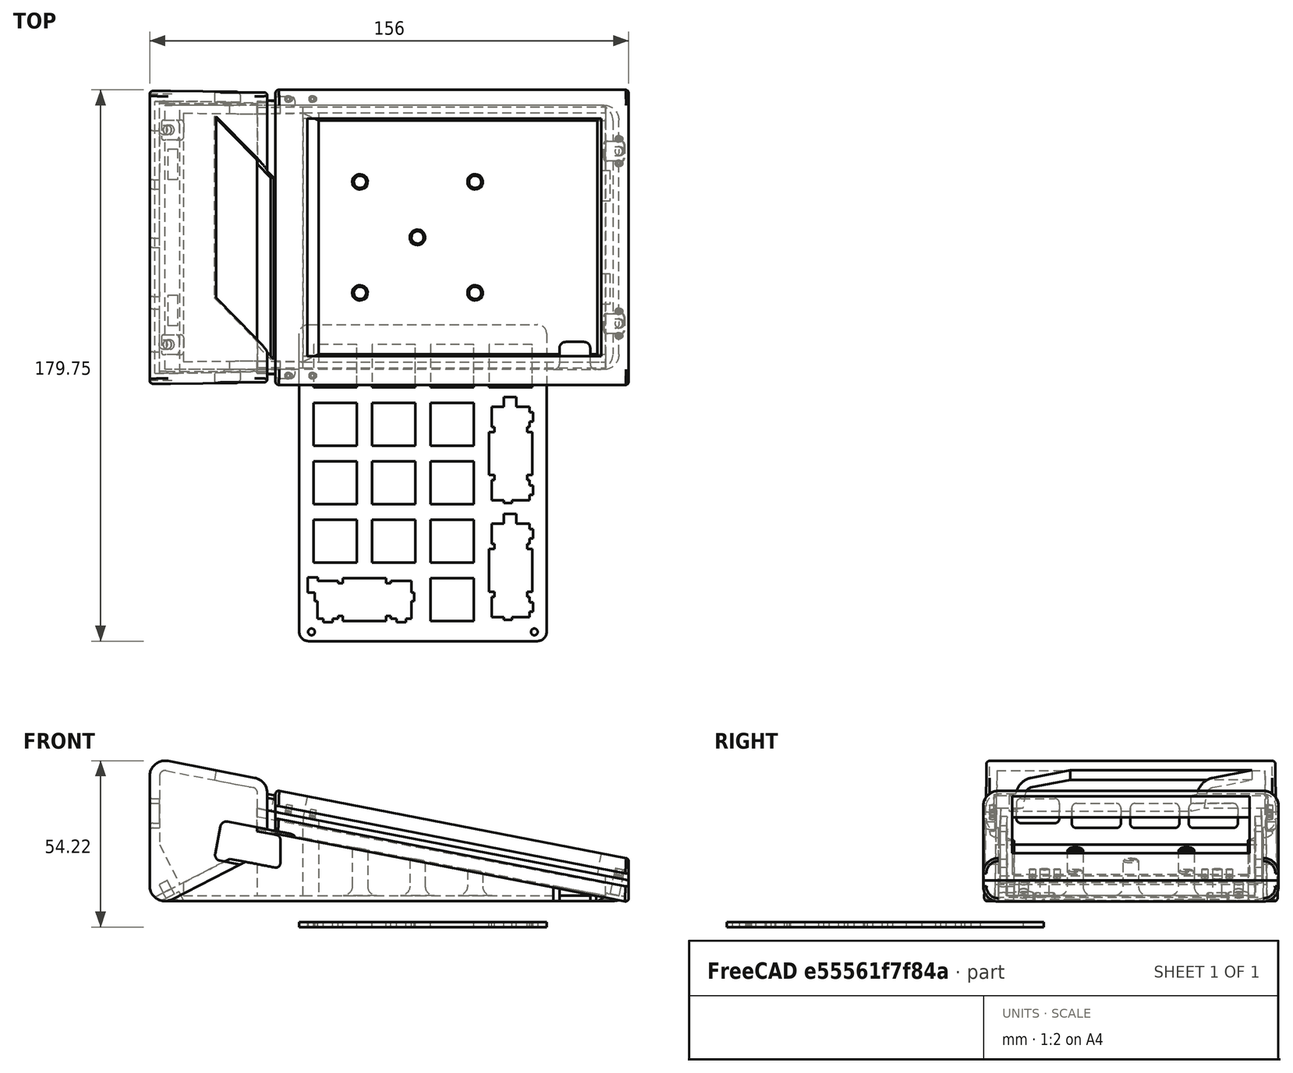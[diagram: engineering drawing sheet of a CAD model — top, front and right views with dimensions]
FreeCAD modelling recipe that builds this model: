
FCSTD DOCUMENT  (FreeCAD 1.0R38806 (Git))
Label: DecenTKL-Numpad-Enclosure
License: All rights reserved
LicenseURL: http://en.wikipedia.org/wiki/All_rights_reserved
objects: Sketcher::SketchObject×35, PartDesign::Pocket×16, PartDesign::Plane×12, PartDesign::Pad×9, PartDesign::SubShapeBinder×8, PartDesign::Point×6, PartDesign::Line×5, Part::Part2DObjectPython×3, App::Part×3, PartDesign::Fillet×3, PartDesign::Body×2, PartDesign::Chamfer×2, PartDesign::Draft×1, Mesh::Feature×1, Part::Feature×1, PartDesign::AdditiveLoft×1, PartDesign::SubtractiveLoft×1
note: 206 computed .brp shape members not serialized (recipe doc carries the construction recipe); baked Part::Feature solids carry a one-line shape summary decoded from their .brp

FEATURE [Sketcher::SketchObject] Sketch  label="ConsoleKeySectionSketch"
  ArcFitTolerance = 0
  AttachmentSupport = -> [XZ_Plane001]
  FullyConstrained = true
  MakeInternals = false
  MapMode = 5
  Placement = pos=(0,0,0) rot=(1,0,0;1.5708rad)
  sketch-geometry (12):
    g0: LineSegment StartX=5.95204 StartY=54.1257 StartZ=0 EndX=34.2385 EndY=48.6393 EndZ=0
    g1: ArcOfCircle CenterX=33.2865 CenterY=43.7308 CenterZ=0 NormalX=0 NormalY=0 NormalZ=1 AngleXU=0 Radius=5 StartAngle=3e-16 EndAngle=1.37922
    g2: LineSegment StartX=38.2865 StartY=43.7308 StartZ=0 EndX=38.2865 EndY=27.9135 EndZ=0
    g3: ArcOfCircle CenterX=33.2865 CenterY=27.9135 CenterZ=0 NormalX=0 NormalY=0 NormalZ=1 AngleXU=0 Radius=5 StartAngle=5.185 EndAngle=6.28319
    g4: LineSegment StartX=35.5625 StartY=23.4615 StartZ=0 EndX=7.27606 EndY=9 EndZ=0
    g5: ArcOfCircle CenterX=5 CenterY=13.4519 CenterZ=0 NormalX=0 NormalY=0 NormalZ=1 AngleXU=0 Radius=5 StartAngle=3.14159 EndAngle=5.185
    g6: LineSegment StartX=1.24e-14 StartY=13.4519 StartZ=0 EndX=1.24e-14 EndY=49.2171 EndZ=0
    g7: ArcOfCircle CenterX=5 CenterY=49.2171 CenterZ=0 NormalX=0 NormalY=0 NormalZ=1 AngleXU=0 Radius=5 StartAngle=1.37922 EndAngle=3.14159
    g8: GeomPoint [constr] X=0 Y=55.2801 Z=0
    g9: GeomPoint [constr] X=38.2865 Y=47.8542 Z=0
    g10: GeomPoint [constr] X=0 Y=5.2801 Z=0
    g11: GeomPoint [constr] X=38.2865 Y=24.8542 Z=0
  constraints (28):
    c: Tangent(g0,g1) = 1.5708
    c: Tangent(g2,g3) = 1.5708
    c: Tangent(g4,g5) = 1.5708
    c: Tangent(g6,g7) = 1.5708
    c: Tangent(g7,g0) = 1.5708
    c: Tangent(g5,g6) = 1.5708
    c: Tangent(g3,g4) = 1.5708
    c: Tangent(g1,g2) = 1.5708
    c: PointOnObject(g8,g0)
    c: PointOnObject(g8,g6)
    c: PointOnObject(g9,g0)
    c: PointOnObject(g9,g2)
    c: PointOnObject(g11,g2)
    c: PointOnObject(g11,g4)
    c: PointOnObject(g10,g4)
    c: PointOnObject(g10,g6)
    c: Distance(g8,g9) = 39
    c: Radius(g1) = 5
    c: Equal(g1,g7)
    c: Equal(g1,g3)
    c: Equal(g1,g5)
    c: Distance(g9,g11) = 23
    c: Distance(g8,g10) = 50
    c: Distance(g10,g11) = 43
    c: Vertical(g6)
    c: Vertical(g2)
    c: DistanceY(g-1,g4) = 9
    c: DistanceX(g-1,g5) = 0
FEATURE [PartDesign::Pad] Pad  label="ConsoleKeySection"
  Direction = (0,-1,2e-16)
  Length = 94
  Length2 = 10
  Placement = pos=(0,0,0) rot=(1,0,0;1.5708rad)
  Profile = -> Sketch
  ReferenceAxis = -> Sketch [N_Axis]
  Suppressed = false
  Type = 0
FEATURE [PartDesign::Draft] Draft  label="KeySectionDraft"
  Angle = 1
  Base = -> Pad [Face10,Face9]
  BaseFeature = -> Pad
  NeutralPlane = -> Pad [Face1]
  Placement = pos=(0,0,0) rot=(1,0,0;1.5708rad)
  SupportTransform = false
  Suppressed = false
FEATURE [PartDesign::Plane] DatumPlane  label="KeyboardSectionBackPlane"
  AttachmentOffset = pos=(0,0,41) rot=(0,0,1;0rad)
  AttachmentSupport = -> [YZ_Plane001]
  Length = 139.608
  MapMode = 2
  Placement = pos=(41,0,0) rot=(0.57735,0.57735,0.57735;2.0944rad)
  ResizeMode = 0
  Width = 98.7235
FEATURE [PartDesign::Line] DatumLine  label="SlopeDatumLineLeft"
  AttacherType = Attacher::AttachEngineLine
  AttachmentSupport = -> [Draft]
  Length = 20
  MapMode = 29
  Placement = pos=(10.3332,-94,53.2759) rot=(0.610836,0.610836,0.503744;2.20832rad)
  ResizeMode = 0
FEATURE [PartDesign::Point] DatumPoint  label="KeyboardSectionBackPlaneAndSlopeIntersectionDatumPointLeft"
  AttacherType = Attacher::AttachEnginePoint
  AttachmentSupport = -> [DatumLine,DatumPlane]
  MapMode = 40
  Placement = pos=(41,-94,47.3279) rot=(0,0,1;0rad)
FEATURE [PartDesign::Line] DatumLine001  label="SlopeDatumLineRight"
  AttacherType = Attacher::AttachEngineLine
  AttachmentSupport = -> [Sketch]
  Length = 20
  MapMode = 29
  Placement = pos=(10.3332,1.18e-14,53.2759) rot=(0.610836,0.610836,0.503744;2.20832rad)
  ResizeMode = 0
FEATURE [PartDesign::Point] DatumPoint001  label="KeyboardSectionBackPlaneAndSlopeIntersectionDatumPointRight"
  AttacherType = Attacher::AttachEnginePoint
  AttachmentSupport = -> [DatumLine001,DatumPlane]
  MapMode = 40
  Placement = pos=(41,1.86e-14,47.3279) rot=(0,0,1;0rad)
FEATURE [Sketcher::SketchObject] Sketch001  label="KeyboardSectionSketch"
  ArcFitTolerance = 0
  AttachmentSupport = -> [DatumPlane]
  ExternalGeometry = -> [DatumPoint,DatumPoint001]
  FullyConstrained = true
  MakeInternals = false
  MapMode = 5
  Placement = pos=(41,0,0) rot=(0.57735,0.57735,0.57735;2.0944rad)
  sketch-geometry (6):
    g0: LineSegment StartX=-95.1 StartY=37.5279 StartZ=0 EndX=1.1 EndY=37.5279 EndZ=0
    g1: LineSegment StartX=1.1 StartY=37.5279 StartZ=0 EndX=1.1 EndY=39.6279 EndZ=0
    g2: LineSegment StartX=-95.1 StartY=37.5279 StartZ=0 EndX=-95.1 EndY=39.6279 EndZ=0
    g3: ArcOfCircle CenterX=-90.1 CenterY=39.6279 CenterZ=0 NormalX=0 NormalY=0 NormalZ=1 AngleXU=0 Radius=5 StartAngle=1.5708 EndAngle=3.14159
    g4: ArcOfCircle CenterX=-3.9 CenterY=39.6279 CenterZ=0 NormalX=0 NormalY=0 NormalZ=1 AngleXU=0 Radius=5 StartAngle=0 EndAngle=1.5708
    g5: LineSegment StartX=-90.1 StartY=44.6279 StartZ=0 EndX=-3.9 EndY=44.6279 EndZ=0
  constraints (20):
    c: Horizontal(g0)
    c: Coincident(g1,g0)
    c: Vertical(g1)
    c: Coincident(g2,g0)
    c: Vertical(g2)
    c: Coincident(g3,g2)
    c: Coincident(g4,g1)
    c: Coincident(g5,g3)
    c: Coincident(g5,g4)
    c: Horizontal(g5)
    c: Vertical(g3,g3)
    c: Vertical(g4,g4)
    c: Horizontal(g2,g3)
    c: Horizontal(g4,g1)
    c: Equal(g2,g1)
    c: Radius(g4) = 5
    c: DistanceX(g2,g-3) = 1.1
    c: DistanceX(g-4,g1) = 1.1
    c: DistanceY(g0,g3) = 7.1
    c: DistanceY(g3,g-3) = 2.7
FEATURE [Sketcher::SketchObject] Sketch002  label="ConsoleToKEyboardSectionJoinSketch"
  ArcFitTolerance = 0
  AttachmentSupport = -> [DatumPlane]
  ExternalGeometry = -> [Sketch001]
  FullyConstrained = true
  MakeInternals = false
  MapMode = 5
  Placement = pos=(41,0,0) rot=(0.57735,0.57735,0.57735;2.0944rad)
  sketch-geometry (8):
    g0: LineSegment StartX=-91.6 StartY=37.5279 StartZ=0 EndX=-2.4 EndY=37.5279 EndZ=0
    g1: LineSegment StartX=-90.4 StartY=42.8279 StartZ=0 EndX=-3.6 EndY=42.8279 EndZ=0
    g2: LineSegment [constr] StartX=-95.1 StartY=37.5279 StartZ=0 EndX=-91.6 EndY=37.5279 EndZ=0
    g3: LineSegment [constr] StartX=-2.4 StartY=37.5279 StartZ=0 EndX=1.1 EndY=37.5279 EndZ=0
    g4: ArcOfCircle CenterX=-90.4 CenterY=41.6279 CenterZ=0 NormalX=0 NormalY=0 NormalZ=1 AngleXU=0 Radius=1.2 StartAngle=1.5708 EndAngle=3.14159
    g5: LineSegment StartX=-91.6 StartY=37.5279 StartZ=0 EndX=-91.6 EndY=41.6279 EndZ=0
    g6: ArcOfCircle CenterX=-3.6 CenterY=41.6279 CenterZ=0 NormalX=0 NormalY=0 NormalZ=1 AngleXU=0 Radius=1.2 StartAngle=1.1e-15 EndAngle=1.5708
    g7: LineSegment StartX=-2.4 StartY=41.6279 StartZ=0 EndX=-2.4 EndY=37.5279 EndZ=0
  constraints (24):
    c: PointOnObject(g0,g-3)
    c: PointOnObject(g0,g-3)
    c: Horizontal(g1)
    c: DistanceX(g-3,g0) = 3.5
    c: Coincident(g2,g-3)
    c: Coincident(g2,g0)
    c: Coincident(g3,g0)
    c: Coincident(g3,g-3)
    c: Vertical(g4,g4)
    c: Coincident(g4,g1)
    c: Vertical(g4,g0)
    c: Horizontal(g4,g4)
    c: Radius(g4) = 1.2
    c: Coincident(g5,g0)
    c: Coincident(g5,g4)
    c: Equal(g4,g6)
    c: Horizontal(g6,g6)
    c: Vertical(g6,g6)
    c: Vertical(g0,g6)
    c: Coincident(g1,g6)
    c: Coincident(g7,g6)
    c: Coincident(g7,g0)
    c: Equal(g2,g3)
    c: DistanceY(g0,g1) = 5.3
FEATURE [PartDesign::Pad] Pad001  label="ConsoleToKeyboardSectionJoin"
  BaseFeature = -> Draft
  Direction = (0.981705,0,-0.190408)
  Length = 10
  Length2 = 10
  Placement = pos=(0,0,0) rot=(1,0,0;1.5708rad)
  Profile = -> Sketch002
  ReferenceAxis = -> DatumLine
  Reversed = true
  Suppressed = false
  Type = 3
  UpToFace = -> Draft [Face3]
FEATURE [PartDesign::Pad] Pad002  label="KeyboardSectionPad"
  BaseFeature = -> Pad001
  Direction = (0.981705,0,-0.190408)
  Length = 115
  Length2 = 10
  Placement = pos=(0,0,0) rot=(1,0,0;1.5708rad)
  Profile = -> Sketch001
  ReferenceAxis = -> DatumLine
  Suppressed = false
  Type = 0
FEATURE [PartDesign::Plane] DatumPlane001  label="ConsoleSectionLeftInnerPlane"
  AttachmentOffset = pos=(0,0,-3.4) rot=(0,0,1;0rad)
  AttachmentSupport = -> [Draft]
  Length = 205.685
  MapMode = 5
  Placement = pos=(0.304171,-91.5189,1.56824) rot=(0.999997,0.00169,0.001662;1.55367rad)
  ResizeMode = 0
  Width = 105.544
FEATURE [PartDesign::Plane] DatumPlane002  label="ConsoleSectionRightInnerPlane"
  AttachmentOffset = pos=(0,0,-3.4) rot=(0,0,1;0rad)
  AttachmentSupport = -> [Draft]
  Length = 205.685
  MapMode = 5
  Placement = pos=(-0.00815113,-2.45251,-0.0420255) rot=(-0.999997,0.00169,-0.001662;1.55367rad)
  ResizeMode = 0
  Width = 105.544
FEATURE [Sketcher::SketchObject] Sketch003  label="ConsoleSectionCavitySketch"
  ArcFitTolerance = 0
  AttachmentOffset = pos=(0,0,10) rot=(0,0,1;0rad)
  AttachmentSupport = -> [XZ_Plane001]
  ExternalGeometry = -> [Sketch,Pad001]
  FullyConstrained = true
  MakeInternals = false
  MapMode = 5
  Placement = pos=(0,-10,2.2e-15) rot=(1,0,0;1.5708rad)
  sketch-geometry (22):
    g0: ArcOfCircle CenterX=5 CenterY=49.2171 CenterZ=0 NormalX=0 NormalY=0 NormalZ=1 AngleXU=0 Radius=1.8 StartAngle=1.37922 EndAngle=3.14159
    g1: LineSegment [constr] StartX=0 StartY=49.2171 StartZ=0 EndX=5 EndY=49.2171 EndZ=0
    g2: LineSegment [constr] StartX=5 StartY=49.2171 StartZ=0 EndX=5.95204 EndY=54.1257 EndZ=0
    g3: LineSegment [constr] StartX=5.95204 StartY=54.1257 StartZ=0 EndX=34.2385 EndY=48.6393 EndZ=0
    g4: LineSegment [constr] StartX=33.2865 StartY=43.7308 StartZ=0 EndX=34.2385 EndY=48.6393 EndZ=0
    g5: LineSegment [constr] StartX=33.2865 StartY=43.7308 StartZ=0 EndX=38.2865 EndY=43.7308 EndZ=0
    g6: ArcOfCircle CenterX=33.2865 CenterY=43.7308 CenterZ=0 NormalX=0 NormalY=0 NormalZ=1 AngleXU=0 Radius=1.8 StartAngle=-8.9e-15 EndAngle=1.37922
    g7: LineSegment StartX=5.34274 StartY=50.9842 StartZ=0 EndX=33.6292 EndY=45.4978 EndZ=0
    g8: LineSegment [constr] StartX=1.24e-14 StartY=13.4519 StartZ=0 EndX=5 EndY=13.4519 EndZ=0
    g9: LineSegment [constr] StartX=5 StartY=13.4519 StartZ=0 EndX=7.27606 EndY=9 EndZ=0
    g10: LineSegment [constr] StartX=33.2865 StartY=27.9135 StartZ=0 EndX=38.2865 EndY=27.9135 EndZ=0
    g11: LineSegment [constr] StartX=33.2865 StartY=27.9135 StartZ=0 EndX=35.5625 EndY=23.4615 EndZ=0
    g12: LineSegment StartX=3.2 StartY=49.2171 StartZ=0 EndX=3.2 EndY=26.8416 EndZ=0
    g13: LineSegment [constr] StartX=7.27606 StartY=9 StartZ=0 EndX=35.5625 EndY=23.4615 EndZ=0
    g14: LineSegment StartX=-17.3575 StartY=0 StartZ=0 EndX=41 EndY=0 EndZ=0
    g15: LineSegment StartX=41 StartY=37.5279 StartZ=0 EndX=41 EndY=0 EndZ=0
    g16: LineSegment StartX=41 StartY=37.5279 StartZ=0 EndX=35.0865 EndY=38.6748 EndZ=0
    g17: LineSegment StartX=35.0865 StartY=38.6748 StartZ=0 EndX=35.0865 EndY=43.7308 EndZ=0
    g18: GeomPoint [constr] X=5.81938 Y=11.8492 Z=0
    g19: LineSegment [constr] StartX=5.81938 StartY=11.8492 StartZ=0 EndX=34.1059 EndY=26.3108 EndZ=0
    g20: LineSegment StartX=-17.3575 StartY=0 StartZ=0 EndX=9.81938 EndY=13.8942 EndZ=0
    g21: LineSegment StartX=3.2 StartY=26.8416 StartZ=0 EndX=9.81938 EndY=13.8942 EndZ=0
  constraints (54):
    c: Coincident(g0,g-3)
    c: Coincident(g1,g-3)
    c: Coincident(g1,g0)
    c: Coincident(g2,g0)
    c: Coincident(g2,g-3)
    c: Coincident(g3,g2)
    c: Coincident(g3,g-4)
    c: Coincident(g4,g-4)
    c: Coincident(g4,g3)
    c: Coincident(g5,g4)
    c: Coincident(g5,g-4)
    c: PointOnObject(g0,g2)
    c: PointOnObject(g0,g1)
    c: DistanceX(g1,g0) = 3.2
    c: Coincident(g6,g4)
    c: PointOnObject(g6,g4)
    c: PointOnObject(g6,g5)
    c: DistanceX(g6,g5) = 3.2
    c: Coincident(g7,g0)
    c: Coincident(g7,g6)
    c: Coincident(g8,g-6)
    c: Coincident(g8,g-6)
    c: Coincident(g9,g8)
    c: Coincident(g9,g-6)
    c: Coincident(g10,g-5)
    c: Coincident(g10,g-5)
    c: Coincident(g11,g10)
    c: Coincident(g11,g-5)
    c: DistanceX(g8,g12) = 3.2
    c: Coincident(g12,g0)
    c: Coincident(g13,g9)
    c: Coincident(g13,g11)
    c: Horizontal(g14)
    c: Coincident(g15,g14)
    c: Vertical(g15)
    c: Coincident(g15,g-7)
    c: Coincident(g16,g15)
    c: Coincident(g17,g16)
    c: Coincident(g17,g6)
    c: Vertical(g17)
    c: PointOnObject(g16,g-7)
    c: PointOnObject(g18,g9)
    c: Distance(g18,g9) = 3.2
    c: Coincident(g19,g18)
    c: PointOnObject(g19,g11)
    c: Parallel(g19,g13)
    c: PointOnObject(g14,g19)
    c: Coincident(g20,g14)
    c: PointOnObject(g14,g-1)
    c: PointOnObject(g20,g19)
    c: Coincident(g21,g12)
    c: Coincident(g21,g20)
    c: Parallel(g21,g9)
    c: DistanceX(g18,g20) = 4
FEATURE [PartDesign::Pocket] Pocket  label="ConsoleKeyCavityPocketRight"
  BaseFeature = -> Pad002
  Direction = (0,1,-2e-16)
  Length = 0
  Length2 = 5
  Placement = pos=(0,0,0) rot=(1,0,0;1.5708rad)
  Profile = -> Sketch003
  ReferenceAxis = -> Sketch003 [N_Axis]
  Refine = true
  Reversed = true
  Suppressed = false
  Type = 3
  UpToFace = -> DatumPlane001 [Plane]
FEATURE [PartDesign::Pocket] Pocket001  label="ConsoleKeyCavityPocketLeft"
  BaseFeature = -> Pocket
  Direction = (0,1,-2e-16)
  Length = 0
  Length2 = 5
  Placement = pos=(0,0,0) rot=(1,0,0;1.5708rad)
  Profile = -> Sketch003
  ReferenceAxis = -> Sketch003 [N_Axis]
  Refine = true
  Suppressed = false
  Type = 3
  UpToFace = -> DatumPlane002 [Plane]
FEATURE [PartDesign::Plane] DatumPlane003  label="KeyboardSlopeDatumPlane"
  AttachmentSupport = -> [DatumLine001,DatumLine]
  Length = 150.532
  MapMode = 13
  Placement = pos=(10.6605,-31.3333,53.2124) rot=(0.095208,0.095208,0.990894;1.57994rad)
  ResizeMode = 0
  Width = 223.203
FEATURE [Sketcher::SketchObject] Sketch004  label="KeyboardCutoutSketch"
  ArcFitTolerance = 0
  AttachmentSupport = -> [DatumPlane003]
  ExternalGeometry = -> [DatumPoint001,DatumPoint]
  FullyConstrained = true
  MakeInternals = false
  MapMode = 5
  Placement = pos=(10.6605,-31.3333,53.2124) rot=(0.095208,0.095208,0.990894;1.57994rad)
  expr: Constraints[23] = 19.05 * 3 + 2
  sketch-geometry (11):
    g0: LineSegment StartX=-54.3917 StartY=-41.9049 StartZ=0 EndX=23.0583 EndY=-41.9049 EndZ=0
    g1: LineSegment StartX=23.0583 StartY=-41.9049 StartZ=0 EndX=23.0583 EndY=-139.505 EndZ=0
    g2: LineSegment StartX=23.0583 StartY=-139.505 StartZ=0 EndX=-54.3917 EndY=-139.505 EndZ=0
    g3: LineSegment StartX=-54.3917 StartY=-139.505 StartZ=0 EndX=-54.3917 EndY=-41.9049 EndZ=0
    g4: GeomPoint [constr] X=-15.6667 Y=-139.505 Z=0
    g5: LineSegment [constr] StartX=-15.6667 StartY=-139.505 StartZ=0 EndX=-15.6667 EndY=-30.9049 EndZ=0
    g6: LineSegment [constr] StartX=-62.6667 StartY=-30.9049 StartZ=0 EndX=31.3333 EndY=-30.9049 EndZ=0
    g7: LineSegment StartX=-55.3917 StartY=-31.2049 StartZ=0 EndX=-35.3917 EndY=-11.2049 EndZ=0
    g8: LineSegment StartX=-35.3917 StartY=-11.2049 StartZ=0 EndX=23.7583 EndY=-11.2049 EndZ=0
    g9: LineSegment StartX=23.7583 StartY=-11.2049 StartZ=0 EndX=3.75833 EndY=-31.2049 EndZ=0
    g10: LineSegment StartX=3.75833 StartY=-31.2049 StartZ=0 EndX=-55.3917 EndY=-31.2049 EndZ=0
  constraints (29):
    c: Horizontal(g0)
    c: Coincident(g0,g1)
    c: Vertical(g1)
    c: Coincident(g3,g0)
    c: Vertical(g3)
    c: DistanceY(g0,g-3) = 11
    c: DistanceY(g2,g0) = 97.6
    c: DistanceX(g0,g0) = 77.45
    c: Coincident(g2,g3)
    c: Coincident(g2,g1)
    c: Coincident(g5,g4)
    c: Coincident(g6,g-4)
    c: Coincident(g6,g-3)
    c: PointOnObject(g5,g6)
    c: Symmetric(g6,g6,g5)
    c: Coincident(g7,g8)
    c: Horizontal(g8)
    c: Coincident(g8,g9)
    c: Coincident(g9,g10)
    c: Coincident(g10,g7)
    c: Horizontal(g10)
    c: Angle(g10,g7) = 0.785398
    c: Angle(g8,g9) = 0.785398
    c: DistanceX(g8,g8) = 59.15
    c: DistanceX(g7,g0) = 1
    c: DistanceY(g9,g8) = 20
    c: Symmetric(g2,g1,g5)
    c: DistanceY(g0,g7) = 10.7
    c: PointOnObject(g4,g2)
FEATURE [PartDesign::Pocket] Pocket002  label="KeyboardCutout"
  BaseFeature = -> Pocket001
  Direction = (-0.190408,-2e-16,-0.981705)
  Length = 10
  Length2 = 5
  Placement = pos=(0,0,0) rot=(1,0,0;1.5708rad)
  Profile = -> Sketch004
  ReferenceAxis = -> Sketch004 [N_Axis]
  Refine = true
  Suppressed = false
  Type = 0
FEATURE [Sketcher::SketchObject] Sketch008  label="Screw holes sketch"
  ArcFitTolerance = 0
  AttachmentSupport = -> [Pad002]
  ExternalGeometry = -> [Pad002]
  FullyConstrained = true
  MakeInternals = false
  MapMode = 5
  Placement = pos=(8.50136,9.8e-15,43.8312) rot=(0.995416,0,-0.095643;3.14159rad)
  sketch-geometry (11):
    g0: Circle CenterX=146.747 CenterY=75.1 CenterZ=0 NormalX=0 NormalY=0 NormalZ=1 AngleXU=0 Radius=1.5
    g1: Circle CenterX=146.747 CenterY=18.9 CenterZ=0 NormalX=0 NormalY=0 NormalZ=1 AngleXU=0 Radius=1.5
    g2: Circle CenterX=146.747 CenterY=79.1 CenterZ=0 NormalX=0 NormalY=0 NormalZ=1 AngleXU=0 Radius=1
    g3: Circle CenterX=146.747 CenterY=71.1 CenterZ=0 NormalX=0 NormalY=0 NormalZ=1 AngleXU=0 Radius=1
    g4: Circle CenterX=37.1043 CenterY=92.1 CenterZ=0 NormalX=0 NormalY=0 NormalZ=1 AngleXU=0 Radius=1
    g5: Circle CenterX=45.1043 CenterY=92.1 CenterZ=0 NormalX=0 NormalY=0 NormalZ=1 AngleXU=0 Radius=1
    g6: Circle CenterX=146.747 CenterY=22.9 CenterZ=0 NormalX=0 NormalY=0 NormalZ=1 AngleXU=0 Radius=1
    g7: Circle CenterX=146.747 CenterY=14.9 CenterZ=0 NormalX=0 NormalY=0 NormalZ=1 AngleXU=0 Radius=1
    g8: Circle CenterX=45.1043 CenterY=1.9 CenterZ=0 NormalX=0 NormalY=0 NormalZ=1 AngleXU=0 Radius=1
    g9: Circle CenterX=37.1043 CenterY=1.9 CenterZ=0 NormalX=0 NormalY=0 NormalZ=1 AngleXU=0 Radius=1
    g10: LineSegment [constr] StartX=33.1043 StartY=47 StartZ=0 EndX=150.247 EndY=47 EndZ=0
  constraints (28):
    c: Vertical(g2,g0)
    c: Symmetric(g2,g3,g0)
    c: DistanceY(g3,g2) = 8
    c: Equal(g2,g3)
    c: Equal(g2,g5)
    c: Equal(g5,g4)
    c: DistanceX(g4,g5) = 8
    c: Vertical(g6,g1)
    c: Symmetric(g6,g7,g1)
    c: DistanceY(g7,g6) = 8
    c: Equal(g6,g7)
    c: Equal(g6,g8)
    c: Equal(g8,g9)
    c: DistanceX(g9,g8) = 8
    c: Symmetric(g0,g1,g10)
    c: Symmetric(g-4,g-3,g10)
    c: Symmetric(g-4,g-3,g10)
    c: DistanceX(g1,g-4) = 3.5
    c: DistanceY(g-4,g1) = 20
    c: Diameter(g5) = 2
    c: Equal(g5,g8)
    c: Horizontal(g9,g8)
    c: Horizontal(g4,g5)
    c: Symmetric(g4,g9,g10)
    c: DistanceY(g9,g4) = 90.2
    c: DistanceX(g-4,g9) = 4
    c: Equal(g0,g1)
    c: Radius(g1) = 1.5
FEATURE [Part::Part2DObjectPython] Shape2DView  label="Key Cutout Projection"  # Draft 2D object (typed FeaturePython)
  AutoUpdate = true
  Base = -> Sketch004
  Clip = false
  FuseArch = false
  HiddenLines = false
  InPlace = true
  OnlySolids = false
  Projection = (0.190408,0,0.981705)
  ProjectionMode = 0
  SegmentLength = 0.05
  Tessellation = false
  VisibleOnly = false
FEATURE [PartDesign::SubShapeBinder] Binder007  label="Slope binder"
  BindCopyOnChange = 0
  BindMode = 0
  ClaimChildren = false
  Context = -> Part001 [Body001.Binder007.]
  Fuse = false
  MakeFace = true
  OffsetFill = false
  OffsetIntersection = false
  OffsetJoinType = 0
  OffsetOpenResult = false
  PartialLoad = false
  Relative = true
  Support = -> [Part[Body.DatumLine001.]]
  _Version = 2
FEATURE [PartDesign::SubShapeBinder] Binder011  label="Top console to keyboard binder"
  BindCopyOnChange = 0
  BindMode = 0
  ClaimChildren = false
  Context = -> Part001 [Body001.Binder011.]
  Fuse = false
  MakeFace = true
  OffsetFill = false
  OffsetIntersection = false
  OffsetJoinType = 0
  OffsetOpenResult = false
  PartialLoad = false
  Relative = true
  Support = -> [Part[Body.Pad001.Face17]]
  _Version = 2
FEATURE [PartDesign::SubShapeBinder] Binder013  label="Screw holes binder"
  BindCopyOnChange = 0
  BindMode = 0
  ClaimChildren = false
  Context = -> Part001 [Body001.Binder013.]
  Fuse = false
  MakeFace = true
  OffsetFill = false
  OffsetIntersection = false
  OffsetJoinType = 0
  OffsetOpenResult = false
  PartialLoad = false
  Relative = true
  Support = -> [Part[Body.Pocket005.Sketch008.]]
  _Version = 2
FEATURE [Mesh::Feature] DecentNumPad
  Placement = pos=(-11.8196,-113,42.0954) rot=(0.095409,0.095409,0.990855;1.57998rad)
FEATURE [Part::Feature] Part__Feature  label="NumPadPlate_PCB"
  shape: bbox 80.58 x 103.2 x 1.6 mm, 178 faces (baked)
FEATURE [App::Part] NumPadPlate_1  label="NumPadPlate 1"
  Group = -> [Part__Feature]
  Origin = -> Origin005
  Placement = pos=(-27.275,-136,49.1) rot=(0.095409,0.095409,0.990855;1.57998rad)
FEATURE [PartDesign::SubShapeBinder] Binder  label="PlateBinder"
  BindCopyOnChange = 0
  BindMode = 0
  ClaimChildren = false
  Context = -> Part [Body.Binder.]
  Fuse = false
  MakeFace = true
  OffsetFill = false
  OffsetIntersection = false
  OffsetJoinType = 0
  OffsetOpenResult = false
  PartialLoad = false
  Relative = true
  Support = -> [NumPadPlate_1[Part__Feature.]]
  _Version = 2
FEATURE [PartDesign::Plane] DatumPlane010  label="TopOfPlatePlane"
  AttachmentSupport = -> [Binder]
  Length = 223.222
  MapMode = 5
  Placement = pos=(8.50886,0,43.7743) rot=(0,1,0;0.191986rad)
  ResizeMode = 0
  Width = 150.533
FEATURE [PartDesign::Line] DatumLine005  label="Right PCB edge"
  AttacherType = Attacher::AttachEngineLine
  AttachmentOffset = pos=(0,-3,0) rot=(0,0,1;0rad)
  AttachmentSupport = -> [Binder]
  Length = 20
  MapMode = 29
  Placement = pos=(7.63113,-6.7,39.2588) rot=(0.610901,0.610901,0.503588;2.20857rad)
  ResizeMode = 0
FEATURE [PartDesign::Line] DatumLine006  label="Left PCB edge"
  AttacherType = Attacher::AttachEngineLine
  AttachmentOffset = pos=(0,-3,0) rot=(0,0,1;0rad)
  AttachmentSupport = -> [Binder]
  Length = 20
  MapMode = 29
  Placement = pos=(7.63113,-87.2812,39.2588) rot=(0.536704,-0.536704,-0.651074;1.98733rad)
  ResizeMode = 0
FEATURE [PartDesign::Plane] DatumPlane011  label="Back plane"
  AttachmentSupport = -> [Pad]
  Length = 98.7235
  MapMode = 5
  Placement = pos=(1.24e-14,0,0) rot=(0.707107,0,-0.707107;3.14159rad)
  ResizeMode = 0
  Width = 139.608
FEATURE [PartDesign::Point] DatumPoint002  label="Back PCB top plane right intersection"
  AttacherType = Attacher::AttachEnginePoint
  AttachmentSupport = -> [DatumPlane011,DatumLine005]
  MapMode = 40
  Placement = pos=(3.6e-15,-6.7,40.7421) rot=(0,0,1;0rad)
FEATURE [PartDesign::Point] DatumPoint003  label="Back PCB top plane left intersection"
  AttacherType = Attacher::AttachEnginePoint
  AttachmentSupport = -> [DatumPlane011,DatumLine006]
  MapMode = 40
  Placement = pos=(3.6e-15,-87.2812,40.7421) rot=(0,0,1;0rad)
FEATURE [Sketcher::SketchObject] Sketch006  label="USB Port Sketch"
  ArcFitTolerance = 0
  AttachmentSupport = -> [Pad]
  ExternalGeometry = -> [DatumPoint003,DatumPoint002]
  FullyConstrained = true
  MakeInternals = false
  MapMode = 5
  Placement = pos=(1.24e-14,0,0) rot=(0.707107,0,-0.707107;3.14159rad)
  sketch-geometry (38):
    g0: ArcOfCircle CenterX=-40.3621 CenterY=82.8112 CenterZ=0 NormalX=0 NormalY=0 NormalZ=1 AngleXU=0 Radius=1.5 StartAngle=1.5708 EndAngle=3.14159
    g1: LineSegment StartX=-40.3621 StartY=84.3112 StartZ=0 EndX=-35.3621 EndY=84.3112 EndZ=0
    g2: ArcOfCircle CenterX=-35.3621 CenterY=82.8112 CenterZ=0 NormalX=0 NormalY=0 NormalZ=1 AngleXU=0 Radius=1.5 StartAngle=-3.6e-15 EndAngle=1.5708
    g3: LineSegment StartX=-33.8621 StartY=82.8112 StartZ=0 EndX=-33.8621 EndY=71.8113 EndZ=0
    g4: ArcOfCircle CenterX=-35.3621 CenterY=71.8112 CenterZ=0 NormalX=0 NormalY=0 NormalZ=1 AngleXU=0 Radius=1.5 StartAngle=4.71239 EndAngle=6.28319
    g5: LineSegment StartX=-35.3621 StartY=70.3112 StartZ=0 EndX=-40.3621 EndY=70.3112 EndZ=0
    g6: ArcOfCircle CenterX=-40.3621 CenterY=71.8112 CenterZ=0 NormalX=0 NormalY=0 NormalZ=1 AngleXU=0 Radius=1.5 StartAngle=3.14159 EndAngle=4.71239
    g7: LineSegment StartX=-41.8621 StartY=71.8112 StartZ=0 EndX=-41.8621 EndY=82.8112 EndZ=0
    g8: GeomPoint [constr] X=-37.8621 Y=77.3112 Z=0
    g9: ArcOfCircle CenterX=-38.7821 CenterY=51.7612 CenterZ=0 NormalX=0 NormalY=0 NormalZ=1 AngleXU=0 Radius=1.5 StartAngle=3.14159 EndAngle=4.71239
    g10: LineSegment StartX=-40.2821 StartY=51.7612 StartZ=0 EndX=-40.2821 EndY=64.7612 EndZ=0
    g11: ArcOfCircle CenterX=-38.7821 CenterY=64.7612 CenterZ=0 NormalX=0 NormalY=0 NormalZ=1 AngleXU=0 Radius=1.5 StartAngle=1.5708 EndAngle=3.14159
    g12: LineSegment StartX=-38.7821 StartY=66.2612 StartZ=0 EndX=-33.7821 EndY=66.2612 EndZ=0
    g13: ArcOfCircle CenterX=-33.7821 CenterY=64.7612 CenterZ=0 NormalX=0 NormalY=0 NormalZ=1 AngleXU=0 Radius=1.5 StartAngle=4.6e-15 EndAngle=1.5708
    g14: LineSegment StartX=-32.2821 StartY=64.7612 StartZ=0 EndX=-32.2821 EndY=51.7612 EndZ=0
    g15: ArcOfCircle CenterX=-33.7821 CenterY=51.7612 CenterZ=0 NormalX=0 NormalY=0 NormalZ=1 AngleXU=0 Radius=1.5 StartAngle=4.71239 EndAngle=6.28319
    g16: LineSegment StartX=-33.7821 StartY=50.2612 StartZ=0 EndX=-38.7821 EndY=50.2612 EndZ=0
    g17: GeomPoint [constr] X=-40.2821 Y=50.2612 Z=0
    g18: GeomPoint [constr] X=-32.2821 Y=66.2613 Z=0
    g19: GeomPoint [constr] X=-36.2821 Y=58.2612 Z=0
    g20: ArcOfCircle CenterX=-38.7821 CenterY=45.7112 CenterZ=0 NormalX=0 NormalY=0 NormalZ=1 AngleXU=0 Radius=1.5 StartAngle=1.5708 EndAngle=3.14159
    g21: LineSegment StartX=-38.7821 StartY=47.2112 StartZ=0 EndX=-33.7821 EndY=47.2112 EndZ=0
    g22: ArcOfCircle CenterX=-33.7821 CenterY=45.7112 CenterZ=0 NormalX=0 NormalY=0 NormalZ=1 AngleXU=0 Radius=1.5 StartAngle=0 EndAngle=1.5708
    g23: LineSegment StartX=-32.2821 StartY=45.7112 StartZ=0 EndX=-32.2821 EndY=32.7112 EndZ=0
    g24: ArcOfCircle CenterX=-33.7821 CenterY=32.7112 CenterZ=0 NormalX=0 NormalY=0 NormalZ=1 AngleXU=0 Radius=1.5 StartAngle=4.71239 EndAngle=6.28319
    g25: LineSegment StartX=-33.7821 StartY=31.2112 StartZ=0 EndX=-38.7821 EndY=31.2112 EndZ=0
    g26: ArcOfCircle CenterX=-38.7821 CenterY=32.7112 CenterZ=0 NormalX=0 NormalY=0 NormalZ=1 AngleXU=0 Radius=1.5 StartAngle=3.14159 EndAngle=4.71239
    g27: LineSegment StartX=-40.2821 StartY=32.7112 StartZ=0 EndX=-40.2821 EndY=45.7112 EndZ=0
    g28: GeomPoint [constr] X=-36.2821 Y=39.2112 Z=0
    g29: ArcOfCircle CenterX=-38.7821 CenterY=26.6612 CenterZ=0 NormalX=0 NormalY=0 NormalZ=1 AngleXU=0 Radius=1.5 StartAngle=1.5708 EndAngle=3.14159
    g30: GeomPoint [constr] X=-36.2821 Y=20.1612 Z=0
    g31: LineSegment StartX=-38.7821 StartY=28.1612 StartZ=0 EndX=-33.7821 EndY=28.1612 EndZ=0
    g32: ArcOfCircle CenterX=-33.7821 CenterY=26.6612 CenterZ=0 NormalX=0 NormalY=0 NormalZ=1 AngleXU=0 Radius=1.5 StartAngle=1e-15 EndAngle=1.5708
    g33: LineSegment StartX=-32.2821 StartY=26.6612 StartZ=0 EndX=-32.2821 EndY=13.6612 EndZ=0
    g34: ArcOfCircle CenterX=-33.7821 CenterY=13.6612 CenterZ=0 NormalX=0 NormalY=0 NormalZ=1 AngleXU=0 Radius=1.5 StartAngle=4.71239 EndAngle=6.28319
    g35: LineSegment StartX=-33.7821 StartY=12.1612 StartZ=0 EndX=-38.7821 EndY=12.1612 EndZ=0
    g36: ArcOfCircle CenterX=-38.7821 CenterY=13.6612 CenterZ=0 NormalX=0 NormalY=0 NormalZ=1 AngleXU=0 Radius=1.5 StartAngle=3.14159 EndAngle=4.71239
    g37: LineSegment StartX=-40.2821 StartY=13.6612 StartZ=0 EndX=-40.2821 EndY=26.6612 EndZ=0
  constraints (88):
    c: Tangent(g0,g1) = 1.5708
    c: Tangent(g1,g2) = 1.5708
    c: Tangent(g2,g3) = 1.5708
    c: Tangent(g3,g4) = 1.5708
    c: Tangent(g4,g5) = 1.5708
    c: Tangent(g5,g6) = 1.5708
    c: Tangent(g6,g7) = 1.5708
    c: Tangent(g7,g0) = 1.5708
    c: Horizontal(g1)
    c: Horizontal(g5)
    c: Vertical(g3)
    c: Vertical(g7)
    c: Equal(g0,g2)
    c: Equal(g2,g4)
    c: Equal(g4,g6)
    c: Diameter(g0) = 3
    c: DistanceX(g6,g3) = 8
    c: DistanceY(g4,g1) = 14
    c: Symmetric(g0,g4,g8)
    c: DistanceX(g-4,g8) = 2.88
    c: Tangent(g9,g10) = 1.5708
    c: Tangent(g10,g11) = 1.5708
    c: Tangent(g11,g12) = 1.5708
    c: Tangent(g12,g13) = 1.5708
    c: Tangent(g13,g14) = 1.5708
    c: Tangent(g14,g15) = 1.5708
    c: Tangent(g15,g16) = 1.5708
    c: Tangent(g16,g9) = 1.5708
    c: Horizontal(g12)
    c: Horizontal(g16)
    c: Vertical(g10)
    c: Vertical(g14)
    c: Equal(g9,g11)
    c: Equal(g11,g13)
    c: Equal(g13,g15)
    c: PointOnObject(g17,g10)
    c: PointOnObject(g17,g16)
    c: PointOnObject(g18,g12)
    c: PointOnObject(g18,g14)
    c: Diameter(g11) = 3
    c: DistanceY(g15,g12) = 16
    c: DistanceX(g10,g13) = 8
    c: Symmetric(g11,g15,g19)
    c: DistanceX(g-4,g19) = 4.46
    c: Tangent(g26,g27) = 1.5708
    c: Tangent(g27,g20) = 1.5708
    c: Tangent(g20,g21) = 1.5708
    c: Tangent(g21,g22) = 1.5708
    c: Tangent(g22,g23) = 1.5708
    c: Tangent(g23,g24) = 1.5708
    c: Tangent(g24,g25) = 1.5708
    c: Tangent(g25,g26) = 1.5708
    c: Horizontal(g21)
    c: Horizontal(g25)
    c: Vertical(g27)
    c: Vertical(g23)
    c: Equal(g26,g20)
    c: Equal(g20,g22)
    c: Equal(g22,g24)
    c: Equal(g11,g20) = 3
    c: Vertical(g10,g26)
    c: Symmetric(g24,g20,g28)
    c: Tangent(g36,g37) = 1.5708
    c: Tangent(g37,g29) = 1.5708
    c: Tangent(g29,g31) = 1.5708
    c: Tangent(g31,g32) = 1.5708
    c: Tangent(g32,g33) = 1.5708
    c: Tangent(g33,g34) = 1.5708
    c: Tangent(g34,g35) = 1.5708
    c: Tangent(g35,g36) = 1.5708
    c: Horizontal(g31)
    c: Horizontal(g35)
    c: Vertical(g37)
    c: Vertical(g33)
    c: Equal(g36,g29)
    c: Equal(g29,g32)
    c: Equal(g32,g34)
    c: Symmetric(g34,g29,g30)
    c: Vertical(g20,g36)
    c: Equal(g29,g20)
    c: Equal(g33,g14)
    c: Equal(g23,g14)
    c: Equal(g21,g12)
    c: Equal(g31,g12)
    c: DistanceY(g8,g-3) = 9.97
    c: DistanceY(g19,g-3) = 29.02
    c: DistanceY(g30,g-3) = 67.12
    c: DistanceY(g28,g-3) = 48.07
FEATURE [PartDesign::Pocket] Pocket004  label="USB Port"
  BaseFeature = -> Pocket002
  Direction = (1,0,2e-16)
  Length = 5
  Length2 = 5
  Placement = pos=(0,0,0) rot=(1,0,0;1.5708rad)
  Profile = -> Sketch006
  Suppressed = false
  Type = 0
FEATURE [PartDesign::Pocket] Pocket005  label="Screw holes"
  BaseFeature = -> Pocket004
  Direction = (0.190408,0,0.981705)
  Length = 3
  Length2 = 5
  Placement = pos=(0,0,0) rot=(1,0,0;1.5708rad)
  Profile = -> Sketch008
  ReferenceAxis = -> Sketch008 [N_Axis]
  Suppressed = false
  Type = 0
FEATURE [PartDesign::Fillet] Fillet
  Base = -> Pocket005 [Edge232,Edge224,Edge216,Edge206,Edge143,Edge194,Edge47,Edge37]
  BaseFeature = -> Pocket005
  Placement = pos=(0,0,0) rot=(1,0,0;1.5708rad)
  Radius = 1
  SupportTransform = false
  Suppressed = false
  UseAllEdges = false
FEATURE [PartDesign::SubShapeBinder] Binder014  label="Plate bottom binder"
  BindCopyOnChange = 0
  BindMode = 0
  ClaimChildren = false
  Context = -> Part001 [Body001.Binder014.]
  Fuse = false
  MakeFace = true
  OffsetFill = false
  OffsetIntersection = false
  OffsetJoinType = 0
  OffsetOpenResult = false
  PartialLoad = false
  Relative = true
  Support = -> [NumPadPlate_1]
  _Version = 2
FEATURE [PartDesign::Plane] DatumPlane012  label="PCB top plane"
  AttachmentOffset = pos=(0,0,3) rot=(0,0,1;0rad)
  AttachmentSupport = -> [Binder014]
  Length = 220.026
  MapMode = 5
  Placement = pos=(7.63113,0,39.2588) rot=(0.995396,0,-0.095846;3.14159rad)
  ResizeMode = 0
  Width = 150.298
FEATURE [Sketcher::SketchObject] Sketch013  label="PCB footprint sketch"
  ArcFitTolerance = 0
  AttachmentSupport = -> [DatumPlane012]
  ExternalGeometry = -> [Binder014]
  FullyConstrained = true
  MakeInternals = false
  MapMode = 5
  Placement = pos=(7.63113,0,39.2588) rot=(0.995396,0,-0.095846;3.14159rad)
  sketch-geometry (4):
    g0: LineSegment StartX=-4.2426 StartY=87.5313 StartZ=0 EndX=142.757 EndY=87.5313 EndZ=0
    g1: LineSegment StartX=142.757 StartY=87.5313 StartZ=0 EndX=142.757 EndY=6.45 EndZ=0
    g2: LineSegment StartX=142.757 StartY=6.45 StartZ=0 EndX=-4.2426 EndY=6.45 EndZ=0
    g3: LineSegment StartX=-4.2426 StartY=6.45 StartZ=0 EndX=-4.2426 EndY=87.5313 EndZ=0
  constraints (12):
    c: Coincident(g0,g1)
    c: Coincident(g1,g2)
    c: Coincident(g2,g3)
    c: Coincident(g3,g0)
    c: Horizontal(g0)
    c: Horizontal(g2)
    c: Vertical(g1)
    c: Vertical(g3)
    c: DistanceX(g-3,g0) = 0.25
    c: DistanceY(g1,g-5) = 0.25
    c: DistanceY(g-4,g0) = 0.25
    c: DistanceX(g2,g2) = 147
FEATURE [PartDesign::Plane] DatumPlane013  label="Middle plane"
  AttachmentSupport = -> [Pad]
  Length = 204.948
  MapMode = 45
  Placement = pos=(34.2385,-47,48.6393) rot=(0,0.707107,0.707107;3.14159rad)
  ResizeMode = 0
  Width = 103.164
FEATURE [Sketcher::SketchObject] Sketch027  label="Joystick port sketch"
  ArcFitTolerance = 0
  AttachmentSupport = -> [XZ_Plane004]
  FullyConstrained = true
  MakeInternals = false
  MapMode = 5
  Placement = pos=(0,0,0) rot=(1,0,0;1.5708rad)
  sketch-geometry (8):
    g0: LineSegment StartX=23.7 StartY=24.5 StartZ=0 EndX=26.4469 EndY=31.6558 EndZ=0
    g1: ArcOfCircle CenterX=27.8472 CenterY=31.1182 CenterZ=0 NormalX=0 NormalY=0 NormalZ=1 AngleXU=0 Radius=1.5 StartAngle=1.37881 EndAngle=2.77507
    g2: LineSegment StartX=28.1334 StartY=32.5907 StartZ=0 EndX=41.3384 EndY=30.0239 EndZ=0
    g3: ArcOfCircle CenterX=41.0521 CenterY=28.5515 CenterZ=0 NormalX=0 NormalY=0 NormalZ=1 AngleXU=0 Radius=1.5 StartAngle=7e-16 EndAngle=1.37881
    g4: LineSegment StartX=42.5521 StartY=28.5515 StartZ=0 EndX=42.5521 EndY=20.8617 EndZ=0
    g5: ArcOfCircle CenterX=41.0521 CenterY=20.8617 CenterZ=0 NormalX=0 NormalY=0 NormalZ=1 AngleXU=0 Radius=1.5 StartAngle=4.5204 EndAngle=6.28319
    g6: LineSegment StartX=40.7659 StartY=19.3893 StartZ=0 EndX=24.8142 EndY=22.49 EndZ=0
    g7: ArcOfCircle CenterX=25.1004 CenterY=23.9624 CenterZ=0 NormalX=0 NormalY=0 NormalZ=1 AngleXU=0 Radius=1.5 StartAngle=2.77507 EndAngle=4.5204
  constraints (20):
    c: Tangent(g0,g1) = 1.5708
    c: Tangent(g2,g3) = 1.5708
    c: Vertical(g4)
    c: Tangent(g4,g5) = 1.5708
    c: Tangent(g6,g7) = 1.5708
    c: DistanceX(g-1,g0) = 23.7
    c: Angle(g6,g-1) = 0.191986
    c: Parallel(g6,g2)
    c: Angle(g6,g0) = 1.39626
    c: Distance(g0,g4) = 19.2
    c: DistanceY(g-1,g0) = 24.5
    c: Radius(g7) = 1.5
    c: Equal(g7,g5)
    c: Equal(g7,g1)
    c: Equal(g7,g3)
    c: Tangent(g1,g2) = 1.5708
    c: Tangent(g3,g4) = 1.5708
    c: Tangent(g5,g6) = 1.5708
    c: Distance(g2,g5) = 10.65
    c: Tangent(g7,g0) = 1.5708
FEATURE [PartDesign::SubShapeBinder] Binder015  label="Screw holes sketch binder"
  BindCopyOnChange = 0
  BindMode = 0
  ClaimChildren = false
  Context = -> Part001 [Body001.Binder015.]
  Fuse = false
  MakeFace = true
  OffsetFill = false
  OffsetIntersection = false
  OffsetJoinType = 0
  OffsetOpenResult = false
  PartialLoad = false
  Relative = true
  Support = -> [Part[Body.Pocket005.Sketch008.]]
  _Version = 2
FEATURE [Sketcher::SketchObject] Sketch030  label="Peg sketch"
  ArcFitTolerance = 0
  ExternalGeometry = -> [Binder015]
  FullyConstrained = false
  MakeInternals = false
  MapMode = 5
  Placement = pos=(158.846,4e-15,14.6709) rot=(-0.095208,0.095208,-0.990894;1.57994rad)
  sketch-geometry (10):
    g0: Circle CenterX=1.9 CenterY=-116.042 CenterZ=0 NormalX=0 NormalY=0 NormalZ=1 AngleXU=0 Radius=1
    g1: Circle CenterX=1.9 CenterY=-108.042 CenterZ=0 NormalX=0 NormalY=0 NormalZ=1 AngleXU=0 Radius=1
    g2: Circle CenterX=14.9 CenterY=-6.39856 CenterZ=0 NormalX=0 NormalY=0 NormalZ=1 AngleXU=0 Radius=1
    g3: Circle CenterX=22.9 CenterY=-6.39856 CenterZ=0 NormalX=0 NormalY=0 NormalZ=1 AngleXU=0 Radius=1
    g4: Circle CenterX=71.1 CenterY=-6.39856 CenterZ=0 NormalX=0 NormalY=0 NormalZ=1 AngleXU=0 Radius=1
    g5: Circle CenterX=79.1 CenterY=-6.39856 CenterZ=0 NormalX=0 NormalY=0 NormalZ=1 AngleXU=0 Radius=1
    g6: Circle CenterX=92.1 CenterY=-108.042 CenterZ=0 NormalX=0 NormalY=0 NormalZ=1 AngleXU=0 Radius=1
    g7: Circle CenterX=92.1 CenterY=-116.042 CenterZ=0 NormalX=0 NormalY=0 NormalZ=1 AngleXU=0 Radius=1
    g8: LineSegment [constr] StartX=14.9 StartY=-6.39856 StartZ=0 EndX=22.9 EndY=-6.39856 EndZ=0
    g9: LineSegment [constr] StartX=71.1 StartY=-6.39856 StartZ=0 EndX=79.1 EndY=-6.39856 EndZ=0
  constraints (13):
    c: Equal(g0,g1)
    c: Equal(g0,g7)
    c: Equal(g0,g6)
    c: Equal(g0, g2-g5) x4
    c: Horizontal(g4,g2)
    c: Horizontal(g5,g4)
    c: Coincident(g8,g2)
    c: Coincident(g8,g3)
    c: Coincident(g9,g4)
    c: Coincident(g9,g5)
    c: Equal(g8,g9)
    c: DistanceX(g1,g2) = 13  'foo'
    c: DistanceX(g5,g6) = 13
FEATURE [Part::Part2DObjectPython] Clone2D  label="Joystick port sketch (2D)"  # Draft 2D object (typed FeaturePython)
  Fuse = false
  Objects = -> [Sketch027]
  Placement = pos=(0,0,0) rot=(1,0,0;1.5708rad)
  Scale = (1,1,1)
FEATURE [Sketcher::SketchObject] Sketch031
  ArcFitTolerance = 0
  AttachmentSupport = -> [DatumPlane013]
  ExternalGeometry = -> [Clone2D]
  FullyConstrained = true
  MakeInternals = false
  MapMode = 5
  Placement = pos=(34.2385,-47,48.6393) rot=(0,0.707107,0.707107;3.14159rad)
  sketch-geometry (12):
    g0: GeomPoint [constr] X=-0.211143 Y=-22.6493 Z=0
    g1: ArcOfCircle CenterX=-11.3769 CenterY=-20.2355 CenterZ=0 NormalX=0 NormalY=0 NormalZ=1 AngleXU=0 Radius=2 StartAngle=1.76278 EndAngle=3.33358
    g2: LineSegment StartX=-11.7585 StartY=-18.2722 StartZ=0 EndX=8.85568 EndY=-14.2652 EndZ=0
    g3: ArcOfCircle CenterX=9.2373 CenterY=-16.2285 CenterZ=0 NormalX=0 NormalY=0 NormalZ=1 AngleXU=0 Radius=2 StartAngle=0.191986 EndAngle=1.76278
    g4: LineSegment StartX=11.2006 StartY=-15.8469 StartZ=0 EndX=12.9178 EndY=-24.6815 EndZ=0
    g5: ArcOfCircle CenterX=10.9546 CenterY=-25.0631 CenterZ=0 NormalX=0 NormalY=0 NormalZ=1 AngleXU=0 Radius=2 StartAngle=4.90438 EndAngle=6.47517
    g6: LineSegment StartX=11.3362 StartY=-27.0264 StartZ=0 EndX=-9.27797 EndY=-31.0334 EndZ=0
    g7: ArcOfCircle CenterX=-9.65959 CenterY=-29.0701 CenterZ=0 NormalX=0 NormalY=0 NormalZ=1 AngleXU=0 Radius=2 StartAngle=3.33358 EndAngle=4.90438
    g8: LineSegment StartX=-11.6228 StartY=-29.4517 StartZ=0 EndX=-13.3401 EndY=-20.6171 EndZ=0
    g9: GeomPoint [constr] X=-13.7217 Y=-18.6538 Z=0
    g10: GeomPoint [constr] X=13.2995 Y=-26.6448 Z=0
    g11: GeomPoint [constr] X=-0.211143 Y=-22.6493 Z=0
  constraints (25):
    c: Symmetric(g-3,g-4,g0)
    c: Tangent(g1,g2) = 1.5708
    c: Tangent(g2,g3) = 1.5708
    c: Tangent(g3,g4) = 1.5708
    c: Tangent(g4,g5) = 1.5708
    c: Tangent(g5,g6) = 1.5708
    c: Tangent(g6,g7) = 1.5708
    c: Tangent(g7,g8) = 1.5708
    c: Tangent(g8,g1) = 1.5708
    c: Equal(g1,g3)
    c: Equal(g3,g5)
    c: Equal(g5,g7)
    c: PointOnObject(g9,g2)
    c: PointOnObject(g9,g8)
    c: PointOnObject(g10,g4)
    c: PointOnObject(g10,g6)
    c: Parallel(g6,g2)
    c: Parallel(g8,g4)
    c: Perpendicular(g4,g6)
    c: Parallel(g-4,g6)
    c: Symmetric(g6,g2,g11)
    c: Coincident(g11,g0)
    c: Radius(g5) = 2
    c: Distance(g1,g3) = 25
    c: Distance(g2,g5) = 13
FEATURE [PartDesign::Pocket] Pocket008  label="Joystick ports001"
  BaseFeature = -> Fillet
  Direction = (0,-1,2e-16)
  Length = 5
  Length2 = 5
  Midplane = true
  Placement = pos=(0,0,0) rot=(1,0,0;1.5708rad)
  Profile = -> Sketch031
  ReferenceAxis = -> Sketch031 [N_Axis]
  Suppressed = false
  Type = 1
FEATURE [Part::Part2DObjectPython] Clone2D001  label="Sketch031 (2D)"  # Draft 2D object (typed FeaturePython)
  Fuse = false
  Objects = -> [Sketch031]
  Placement = pos=(34.2385,-47,48.6393) rot=(0,0.707107,0.707107;3.14159rad)
  Scale = (1,1,1)
FEATURE [Sketcher::SketchObject] Sketch034  label="Back screws holes"
  ArcFitTolerance = 0
  AttachmentSupport = -> [Pocket008]
  ExternalGeometry = -> [Pocket008]
  FullyConstrained = true
  MakeInternals = false
  MapMode = 5
  Placement = pos=(-3.59676,3.1e-15,7.0352) rot=(0.97221,0,0.234112;3.14159rad)
  sketch-geometry (3):
    g0: GeomPoint [constr] X=10.4892 Y=46.9507 Z=0
    g1: Circle CenterX=10.4892 CenterY=81.9507 CenterZ=0 NormalX=0 NormalY=0 NormalZ=1 AngleXU=0 Radius=1.5
    g2: Circle CenterX=10.4892 CenterY=11.9507 CenterZ=0 NormalX=0 NormalY=0 NormalZ=1 AngleXU=0 Radius=1.5
  constraints (6):
    c: Symmetric(g-4,g-3,g0)
    c: Vertical(g1,g0)
    c: Equal(g1,g2)
    c: Diameter(g1) = 3
    c: DistanceY(g2,g1) = 70
    c: Symmetric(g1,g2,g0)
FEATURE [PartDesign::Pocket] Pocket012  label="Back screw holes"
  BaseFeature = -> Pocket008
  Direction = (-0.455211,0,0.890384)
  Length = 3
  Length2 = 5
  Placement = pos=(0,0,0) rot=(1,0,0;1.5708rad)
  Profile = -> Sketch034
  ReferenceAxis = -> Sketch034 [N_Axis]
  Suppressed = false
  Type = 0
FEATURE [PartDesign::Body] Body  label="EnclosureTopBody"
  AllowCompound = false
  Group = -> [Sketch,Pad,Draft,DatumPlane,Sketch001,DatumLine,DatumPoint,DatumLine001,DatumPoint001,Sketch002,Pad001,Pad002,DatumPlane001,DatumPlane002,Sketch003,Pocket,Pocket001,DatumPlane003,Sketch004,Pocket002,Sketch006,Pocket004,Sketch008,Pocket005,Fillet,Binder,DatumPlane010,DatumLine005,DatumLine006,DatumPlane011,DatumPoint002,DatumPoint003,DatumPlane013,Clone2D,Sketch031,Pocket008,Sketch034,Pocket012]
  Origin = -> Origin001
  Tip = -> Pocket012
FEATURE [App::Part] Part  label="EnclosureTop"
  Group = -> [Body]
  Origin = -> Origin
FEATURE [PartDesign::SubShapeBinder] Binder016  label="Back screws binder"
  BindCopyOnChange = 0
  BindMode = 0
  ClaimChildren = false
  Context = -> Part001 [Body001.Binder016.]
  Fuse = false
  MakeFace = true
  OffsetFill = false
  OffsetIntersection = false
  OffsetJoinType = 0
  OffsetOpenResult = false
  PartialLoad = false
  Relative = true
  Support = -> [Part[Body.Pocket012.Sketch034.]]
  _Version = 2
FEATURE [PartDesign::SubShapeBinder] Binder017
  BindCopyOnChange = 0
  BindMode = 0
  ClaimChildren = false
  Context = -> Part001 [Body001.Binder017.]
  Fuse = false
  MakeFace = true
  OffsetFill = false
  OffsetIntersection = false
  OffsetJoinType = 0
  OffsetOpenResult = false
  PartialLoad = false
  Relative = true
  Support = -> [Part[Body.Pocket001.]]
  _Version = 2
FEATURE [PartDesign::Plane] DatumPlane005  label="Case front datum plane"
  AttachmentSupport = -> [Binder017]
  Length = 137.592
  MapMode = 5
  Placement = pos=(156,0,0) rot=(0.57735,0.57735,0.57735;2.0944rad)
  ResizeMode = 0
  Width = 81.1837
FEATURE [Sketcher::SketchObject] Sketch010  label="Keyboard section sketch"
  ArcFitTolerance = 0
  AttachmentSupport = -> [DatumPlane005]
  FullyConstrained = false
  MakeInternals = false
  MapMode = 5
  Placement = pos=(156,0,0) rot=(0.57735,0.57735,0.57735;2.0944rad)
  sketch-geometry (7):
    g0: LineSegment StartX=-95.1 StartY=15.2228 StartZ=0 EndX=1.1 EndY=15.2228 EndZ=0
    g1: LineSegment StartX=1.1 StartY=15.2228 StartZ=0 EndX=1.1 EndY=13.1228 EndZ=0
    g2: ArcOfCircle CenterX=-3.9 CenterY=13.1228 CenterZ=0 NormalX=0 NormalY=0 NormalZ=1 AngleXU=0 Radius=5 StartAngle=4.71239 EndAngle=6.28319
    g3: LineSegment StartX=-3.9 StartY=8.12284 StartZ=0 EndX=-90.1 EndY=8.12284 EndZ=0
    g4: ArcOfCircle CenterX=-90.1 CenterY=13.1228 CenterZ=0 NormalX=0 NormalY=0 NormalZ=1 AngleXU=0 Radius=5 StartAngle=3.14159 EndAngle=4.71239
    g5: LineSegment StartX=-95.1 StartY=13.1228 StartZ=0 EndX=-95.1 EndY=15.2228 EndZ=0
    g6: LineSegment [constr] StartX=-95.1 StartY=17.3228 StartZ=0 EndX=-95.1 EndY=15.2228 EndZ=0
  constraints (13):
    c: Coincident(g0,g1)
    c: Vertical(g1)
    c: Tangent(g1,g2) = 1.5708
    c: Coincident(g2,g3)
    c: Horizontal(g3)
    c: Tangent(g3,g4) = 1.5708
    c: Coincident(g4,g5)
    c: Coincident(g5,g0)
    c: Vertical(g5)
    c: Horizontal(g4,g4)
    c: Vertical(g2,g2)
    c: Coincident(g6,g0)
    c: Equal(g6,g5)
FEATURE [PartDesign::Pad] Pad004  label="Keyboard pad"
  Direction = (0.981705,2e-16,-0.190408)
  Length = 115
  Length2 = 10
  Placement = pos=(156,0,0) rot=(0.57735,0.57735,0.57735;2.0944rad)
  Profile = -> Sketch010
  ReferenceAxis = -> Binder007 [Edge1]
  Reversed = true
  Suppressed = false
  Type = 0
FEATURE [Sketcher::SketchObject] Sketch011  label="Bottom hidden extra thickness sketch 1"
  ArcFitTolerance = 0
  AttachmentSupport = -> [Pad004]
  ExternalGeometry = -> [Pad004]
  FullyConstrained = true
  MakeInternals = false
  MapMode = 5
  Placement = pos=(157.518,-1e-16,7.82834) rot=(0.70548,0.70548,-0.067785;3.27696rad)
  sketch-geometry (7):
    g0: ArcOfCircle CenterX=-85.1 CenterY=-9.74666 CenterZ=0 NormalX=0 NormalY=0 NormalZ=1 AngleXU=0 Radius=5 StartAngle=1.5708 EndAngle=3.14159
    g1: ArcOfCircle CenterX=-8.9 CenterY=-9.74666 CenterZ=0 NormalX=0 NormalY=0 NormalZ=1 AngleXU=0 Radius=5 StartAngle=0 EndAngle=1.5708
    g2: LineSegment StartX=-3.9 StartY=-9.74666 StartZ=0 EndX=-3.9 EndY=-118.69 EndZ=0
    g3: LineSegment StartX=-3.9 StartY=-118.69 StartZ=0 EndX=-90.1 EndY=-118.69 EndZ=0
    g4: LineSegment StartX=-90.1 StartY=-118.69 StartZ=0 EndX=-90.1 EndY=-9.74666 EndZ=0
    g5: GeomPoint [constr] X=-3.9 Y=-118.69 Z=0
    g6: LineSegment StartX=-85.1 StartY=-4.74666 StartZ=0 EndX=-8.9 EndY=-4.74666 EndZ=0
  constraints (19):
    c: Vertical(g2)
    c: Vertical(g4)
    c: Equal(g0,g1)
    c: Radius(g0) = 5
    c: Coincident(g3,g5)
    c: Coincident(g2,g3)
    c: Coincident(g2,g-4)
    c: Coincident(g3,g-3)
    c: Coincident(g4,g3)
    c: Coincident(g0,g4)
    c: Horizontal(g0,g0)
    c: Vertical(g0,g0)
    c: Coincident(g1,g2)
    c: Vertical(g1,g1)
    c: Coincident(g6,g0)
    c: Coincident(g6,g1)
    c: Horizontal(g6)
    c: Horizontal(g1,g1)
    c: DistanceY(g0,g-3) = 3.2
FEATURE [Sketcher::SketchObject] Sketch012  label="Bottom hidden extra thickness sketch 2"
  ArcFitTolerance = 0
  AttachmentOffset = pos=(0,0,8.45) rot=(0,0,1;-1.5708rad)
  AttachmentSupport = -> [XY_Plane004]
  ExternalGeometry = -> [Sketch011]
  FullyConstrained = true
  MakeInternals = false
  MapMode = 5
  Placement = pos=(0,0,8.45) rot=(0,0,1;4.71239rad)
  sketch-geometry (6):
    g0: LineSegment StartX=8.9 StartY=150.95 StartZ=0 EndX=85.1 EndY=150.95 EndZ=0
    g1: LineSegment StartX=90.1 StartY=5 StartZ=0 EndX=3.9 EndY=5 EndZ=0
    g2: ArcOfCircle CenterX=8.9 CenterY=145.95 CenterZ=0 NormalX=0 NormalY=0 NormalZ=1 AngleXU=0 Radius=5 StartAngle=1.5708 EndAngle=3.14159
    g3: ArcOfCircle CenterX=85.1 CenterY=145.95 CenterZ=0 NormalX=0 NormalY=0 NormalZ=1 AngleXU=0 Radius=5 StartAngle=0 EndAngle=1.5708
    g4: LineSegment StartX=3.9 StartY=145.95 StartZ=0 EndX=3.9 EndY=5 EndZ=0
    g5: LineSegment StartX=90.1 StartY=145.95 StartZ=0 EndX=90.1 EndY=5 EndZ=0
  constraints (20):
    c: Coincident(g2,g0)
    c: Coincident(g3,g0)
    c: Vertical(g0,g3)
    c: Vertical(g0,g2)
    c: Vertical(g2,g1)
    c: Vertical(g3,g1)
    c: Horizontal(g2,g2)
    c: Horizontal(g3,g3)
    c: Coincident(g4,g2)
    c: Coincident(g5,g3)
    c: Coincident(g5,g1)
    c: Coincident(g4,g1)
    c: Equal(g2,g3)
    c: Horizontal(g0)
    c: Horizontal(g1)
    c: Radius(g3) = 5
    c: Vertical(g-6,g1)
    c: Vertical(g-5,g1)
    c: DistanceY(g2,g-4) = 2
    c: DistanceY(g-1,g1) = 5
FEATURE [PartDesign::AdditiveLoft] AdditiveLoft  label="Bottom hidden extra thickness"
  BaseFeature = -> Pad004
  Closed = false
  Placement = pos=(156,0,0) rot=(0.57735,0.57735,0.57735;2.0944rad)
  Profile = -> Sketch011
  Ruled = true
  Sections = -> [Sketch012]
  Suppressed = false
FEATURE [Sketcher::SketchObject] Sketch014  label="Bottom console to keyboard sketch"
  ArcFitTolerance = 0
  AttachmentSupport = -> [AdditiveLoft]
  ExternalGeometry = -> [Binder011,AdditiveLoft]
  FullyConstrained = true
  MakeInternals = false
  MapMode = 5
  Placement = pos=(41,0,0) rot=(0.57735,0.57735,-0.57735;4.18879rad)
  sketch-geometry (8):
    g0: LineSegment StartX=-91.35 StartY=-37.5279 StartZ=0 EndX=-91.35 EndY=-30.5866 EndZ=0
    g1: LineSegment StartX=-90.1 StartY=-8.45 StartZ=0 EndX=-3.9 EndY=-8.45 EndZ=0
    g2: LineSegment StartX=-2.65 StartY=-30.5866 StartZ=0 EndX=-2.65 EndY=-37.5279 EndZ=0
    g3: LineSegment StartX=-2.65 StartY=-37.5279 StartZ=0 EndX=-91.35 EndY=-37.5279 EndZ=0
    g4: ArcOfCircle CenterX=-90.1 CenterY=-35.4279 CenterZ=0 NormalX=0 NormalY=0 NormalZ=1 AngleXU=0 Radius=5 StartAngle=1.5708 EndAngle=1.82348
    g5: LineSegment StartX=-90.1 StartY=-30.4279 StartZ=0 EndX=-90.1 EndY=-8.45 EndZ=0
    g6: LineSegment StartX=-3.9 StartY=-8.45 StartZ=0 EndX=-3.9 EndY=-30.4279 EndZ=0
    g7: ArcOfCircle CenterX=-3.9 CenterY=-35.4279 CenterZ=0 NormalX=0 NormalY=0 NormalZ=1 AngleXU=0 Radius=5 StartAngle=1.31812 EndAngle=1.5708
  constraints (20):
    c: Vertical(g0)
    c: Coincident(g1,g-5)
    c: Vertical(g2)
    c: Coincident(g4,g-5)
    c: Coincident(g0,g4)
    c: Coincident(g4,g-7)
    c: Coincident(g5,g4)
    c: Coincident(g5,g1)
    c: Coincident(g6,g1)
    c: Coincident(g6,g-8)
    c: Coincident(g7,g-8)
    c: Coincident(g7,g6)
    c: Coincident(g7,g2)
    c: Coincident(g1,g-6)
    c: Horizontal(g3)
    c: DistanceX(g-4,g3) = 0.25
    c: Coincident(g0,g3)
    c: Coincident(g2,g3)
    c: Horizontal(g-4,g0)
    c: DistanceX(g2,g-3) = 0.25
FEATURE [PartDesign::Pad] Pad005  label="Bottom console to keyboard"
  BaseFeature = -> AdditiveLoft
  Direction = (0.981705,0,-0.190408)
  Length = 6
  Length2 = 10
  Placement = pos=(156,0,0) rot=(0.57735,0.57735,0.57735;2.0944rad)
  Profile = -> Sketch014
  ReferenceAxis = -> Binder007 [Edge1]
  Refine = true
  Reversed = true
  Suppressed = false
  Type = 0
FEATURE [PartDesign::Plane] DatumPlane009  label="Base horizontal plane"
  AttachmentSupport = -> [AdditiveLoft]
  Length = 218.45
  MapMode = 45
  Placement = pos=(151.904,-47,8.59107) rot=(0,-1,0;0.14677rad)
  ResizeMode = 0
  Width = 150.182
FEATURE [PartDesign::Plane] DatumPlane014  label="Middle plane for bottom"
  AttachmentSupport = -> [Pad005]
  Length = 202.474
  MapMode = 45
  Placement = pos=(156,-47,15.2228) rot=(0,0.707107,0.707107;3.14159rad)
  ResizeMode = 0
  Width = 85.1655
FEATURE [Sketcher::SketchObject] Sketch015  label="Console bottom sketch"
  ArcFitTolerance = 0
  AttachmentSupport = -> [DatumPlane014]
  ExternalGeometry = -> [AdditiveLoft]
  FullyConstrained = false
  MakeInternals = false
  MapMode = 5
  Placement = pos=(156,-47,15.2228) rot=(0,0.707107,0.707107;3.14159rad)
  sketch-geometry (9):
    g0: ArcOfCircle CenterX=122.709 CenterY=12.702 CenterZ=0 NormalX=0 NormalY=0 NormalZ=1 AngleXU=0 Radius=1.78909 StartAngle=3.14159 EndAngle=4.23926
    g1: LineSegment StartX=121.894 StartY=11.1095 StartZ=0 EndX=154.334 EndY=-5.49706 EndZ=0
    g2: LineSegment StartX=117.72 StartY=22.702 StartZ=0 EndX=117.72 EndY=12.702 EndZ=0
    g3: ArcOfCircle CenterX=122.709 CenterY=12.702 CenterZ=0 NormalX=0 NormalY=0 NormalZ=1 AngleXU=0 Radius=4.98909 StartAngle=3.14159 EndAngle=4.23926
    g4: ArcOfCircle CenterX=151.004 CenterY=-1.78229 CenterZ=0 NormalX=0 NormalY=0 NormalZ=1 AngleXU=0 Radius=4.98909 StartAngle=4.23926 EndAngle=5.44328
    g5: LineSegment StartX=120.436 StartY=8.26102 StartZ=0 EndX=148.73 EndY=-6.22331 EndZ=0
    g6: LineSegment StartX=120.92 StartY=12.702 StartZ=0 EndX=120.92 EndY=22.702 EndZ=0
    g7: LineSegment StartX=117.72 StartY=22.702 StartZ=0 EndX=120.92 EndY=22.702 EndZ=0
    g8: LineSegment [constr] StartX=120.436 StartY=8.26102 StartZ=0 EndX=122.709 EndY=12.702 EndZ=0
  constraints (19):
    c: Coincident(g3,g0)
    c: Horizontal(g0,g0)
    c: Coincident(g6,g0)
    c: Vertical(g6)
    c: Horizontal(g2,g6)
    c: Coincident(g7,g2)
    c: Coincident(g7,g6)
    c: DistanceX(g7,g7) = 3.2
    c: Parallel(g5,g1)
    c: Distance(g3,g0) = 3.2
    c: Coincident(g8,g3)
    c: Coincident(g8,g0)
    c: Equal(g3,g4)
    c: Coincident(g1,g4)
    c: Tangent(g5,g4) = -1.5708
    c: Tangent(g5,g3) = -1.5708
    c: Tangent(g1,g0) = -1.5708
    c: DistanceY(g2,g2) = 10
    c: Tangent(g3,g2) = -1.5708
FEATURE [PartDesign::Pad] Pad006  label="Console bottom to left side"
  BaseFeature = -> Pad005
  Direction = (0,1,-2e-16)
  Length = 10
  Length2 = 10
  Placement = pos=(156,0,0) rot=(0.57735,0.57735,0.57735;2.0944rad)
  Profile = -> Sketch015
  ReferenceAxis = -> Sketch015 [N_Axis]
  Suppressed = false
  Type = 3
  UpToFace = -> Binder017 [Face8]
FEATURE [PartDesign::Pad] Pad007  label="Console bottom to right side"
  BaseFeature = -> Pad006
  Direction = (0,1,-2e-16)
  Length = 10
  Length2 = 10
  Placement = pos=(156,0,0) rot=(0.57735,0.57735,0.57735;2.0944rad)
  Profile = -> Sketch015
  ReferenceAxis = -> Sketch015 [N_Axis]
  Refine = true
  Suppressed = false
  Type = 3
  UpToFace = -> Binder017 [Face17]
FEATURE [Sketcher::SketchObject] Sketch017  label="Bottom screw hole sketch"
  ArcFitTolerance = 0
  AttachmentSupport = -> [Pad007]
  ExternalGeometry = -> [Binder013]
  FullyConstrained = true
  MakeInternals = false
  MapMode = 5
  Placement = pos=(158.846,-4.4e-15,14.6709) rot=(-0.095208,0.095208,-0.990894;1.57994rad)
  sketch-geometry (2):
    g0: Circle CenterX=18.9 CenterY=-6.39856 CenterZ=0 NormalX=0 NormalY=0 NormalZ=1 AngleXU=0 Radius=1.5
    g1: Circle CenterX=75.1 CenterY=-6.39856 CenterZ=0 NormalX=0 NormalY=0 NormalZ=1 AngleXU=0 Radius=1.5
  constraints (4):
    c: Coincident(g0,g-4)
    c: Coincident(g1,g-3)
    c: Equal(g0,g-4)
    c: Equal(g-3,g1)
FEATURE [Sketcher::SketchObject] Sketch018  label="Position helpers sketch"
  ArcFitTolerance = 0
  AttachmentSupport = -> [Pad007]
  ExternalGeometry = -> [Binder013]
  FullyConstrained = true
  MakeInternals = false
  MapMode = 5
  Placement = pos=(158.846,-4.4e-15,14.6709) rot=(-0.095208,0.095208,-0.990894;1.57994rad)
  sketch-geometry (8):
    g0: Circle CenterX=22.9 CenterY=-6.39856 CenterZ=0 NormalX=0 NormalY=0 NormalZ=1 AngleXU=0 Radius=1
    g1: Circle CenterX=92.1 CenterY=-116.042 CenterZ=0 NormalX=0 NormalY=0 NormalZ=1 AngleXU=0 Radius=1
    g2: Circle CenterX=1.9 CenterY=-116.042 CenterZ=0 NormalX=0 NormalY=0 NormalZ=1 AngleXU=0 Radius=1
    g3: Circle CenterX=79.1 CenterY=-6.39856 CenterZ=0 NormalX=0 NormalY=0 NormalZ=1 AngleXU=0 Radius=1
    g4: Circle CenterX=92.1 CenterY=-108.042 CenterZ=0 NormalX=0 NormalY=0 NormalZ=1 AngleXU=0 Radius=1
    g5: Circle CenterX=1.9 CenterY=-108.042 CenterZ=0 NormalX=0 NormalY=0 NormalZ=1 AngleXU=0 Radius=1
    g6: Circle CenterX=71.1 CenterY=-6.39856 CenterZ=0 NormalX=0 NormalY=0 NormalZ=1 AngleXU=0 Radius=1
    g7: Circle CenterX=14.9 CenterY=-6.39856 CenterZ=0 NormalX=0 NormalY=0 NormalZ=1 AngleXU=0 Radius=1
  constraints (16):
    c: Equal(g5,g4)
    c: Equal(g4,g3)
    c: Equal(g3,g2)
    c: Equal(g0,g1)
    c: Equal(g0,g2)
    c: Equal(g6,g7)
    c: Equal(g6,g1)
    c: Coincident(g0,g-4)
    c: Coincident(g7,g-3)
    c: Coincident(g6,g-5)
    c: Coincident(g3,g-6)
    c: Coincident(g5,g-7)
    c: Coincident(g2,g-8)
    c: Coincident(g4,g-9)
    c: Coincident(g1,g-10)
    c: Equal(g-3,g7)
FEATURE [Sketcher::SketchObject] Sketch019  label="Screw head base sketch"
  ArcFitTolerance = 0
  AttachmentSupport = -> [Pad007]
  ExternalGeometry = -> [Sketch017]
  FullyConstrained = true
  MakeInternals = false
  MapMode = 5
  Placement = pos=(157.518,-2e-15,7.82834) rot=(0.70548,0.70548,-0.067785;3.27696rad)
  sketch-geometry (16):
    g0: ArcOfCircle CenterX=-20.9 CenterY=-4.39856 CenterZ=0 NormalX=0 NormalY=0 NormalZ=1 AngleXU=0 Radius=1.5 StartAngle=1.5708 EndAngle=3.14159
    g1: LineSegment StartX=-20.9 StartY=-2.89856 StartZ=0 EndX=-16.9 EndY=-2.89856 EndZ=0
    g2: ArcOfCircle CenterX=-16.9 CenterY=-4.39856 CenterZ=0 NormalX=0 NormalY=0 NormalZ=1 AngleXU=0 Radius=1.5 StartAngle=-1.12816e-11 EndAngle=1.5708
    g3: LineSegment StartX=-15.4 StartY=-4.39856 StartZ=0 EndX=-15.4 EndY=-8.39856 EndZ=0
    g4: ArcOfCircle CenterX=-16.9 CenterY=-8.39856 CenterZ=0 NormalX=0 NormalY=0 NormalZ=1 AngleXU=0 Radius=1.5 StartAngle=4.71239 EndAngle=6.28319
    g5: LineSegment StartX=-16.9 StartY=-9.89856 StartZ=0 EndX=-20.9 EndY=-9.89856 EndZ=0
    g6: ArcOfCircle CenterX=-20.9 CenterY=-8.39856 CenterZ=0 NormalX=0 NormalY=0 NormalZ=1 AngleXU=0 Radius=1.5 StartAngle=3.14159 EndAngle=4.71239
    g7: LineSegment StartX=-22.4 StartY=-8.39856 StartZ=0 EndX=-22.4 EndY=-4.39856 EndZ=0
    g8: ArcOfCircle CenterX=-77.1 CenterY=-4.39856 CenterZ=0 NormalX=0 NormalY=0 NormalZ=1 AngleXU=0 Radius=1.5 StartAngle=1.5708 EndAngle=3.14159
    g9: LineSegment StartX=-77.1 StartY=-2.89856 StartZ=0 EndX=-73.1 EndY=-2.89856 EndZ=0
    g10: ArcOfCircle CenterX=-73.1 CenterY=-4.39856 CenterZ=0 NormalX=0 NormalY=0 NormalZ=1 AngleXU=0 Radius=1.5 StartAngle=0 EndAngle=1.5708
    g11: LineSegment StartX=-71.6 StartY=-4.39856 StartZ=0 EndX=-71.6 EndY=-8.39856 EndZ=0
    g12: ArcOfCircle CenterX=-73.1 CenterY=-8.39856 CenterZ=0 NormalX=0 NormalY=0 NormalZ=1 AngleXU=0 Radius=1.5 StartAngle=4.71239 EndAngle=6.28319
    g13: LineSegment StartX=-73.1 StartY=-9.89856 StartZ=0 EndX=-77.1 EndY=-9.89856 EndZ=0
    g14: ArcOfCircle CenterX=-77.1 CenterY=-8.39856 CenterZ=0 NormalX=0 NormalY=0 NormalZ=1 AngleXU=0 Radius=1.5 StartAngle=3.14159 EndAngle=4.71239
    g15: LineSegment StartX=-78.6 StartY=-8.39856 StartZ=0 EndX=-78.6 EndY=-4.39856 EndZ=0
  constraints (38):
    c: Tangent(g0,g1) = 1.5708
    c: Tangent(g1,g2) = 1.5708
    c: Tangent(g2,g3) = 1.5708
    c: Tangent(g3,g4) = 1.5708
    c: Tangent(g4,g5) = 1.5708
    c: Tangent(g5,g6) = 1.5708
    c: Tangent(g6,g7) = 1.5708
    c: Tangent(g7,g0) = 1.5708
    c: Horizontal(g1)
    c: Horizontal(g5)
    c: Vertical(g3)
    c: Vertical(g7)
    c: Equal(g0,g2)
    c: Equal(g2,g4)
    c: Equal(g4,g6)
    c: Equal(g1,g3)
    c: Tangent(g8,g9) = 1.5708
    c: Tangent(g9,g10) = 1.5708
    c: Tangent(g10,g11) = 1.5708
    c: Tangent(g11,g12) = 1.5708
    c: Tangent(g12,g13) = 1.5708
    c: Tangent(g13,g14) = 1.5708
    c: Tangent(g14,g15) = 1.5708
    c: Tangent(g15,g8) = 1.5708
    c: Horizontal(g9)
    c: Horizontal(g13)
    c: Vertical(g11)
    c: Vertical(g15)
    c: Equal(g8,g10)
    c: Equal(g10,g12)
    c: Equal(g12,g14)
    c: Equal(g13,g11)
    c: Radius(g2) = 1.5
    c: Equal(g2,g10)
    c: Equal(g9,g1)
    c: DistanceX(g8,g10) = 7
    c: Symmetric(g14,g10,g-3)
    c: Symmetric(g6,g2,g-4)
FEATURE [Sketcher::SketchObject] Sketch020  label="Feet sketch"
  ArcFitTolerance = 0
  AttachmentSupport = -> [DatumPlane009]
  ExternalGeometry = -> [Pad007]
  FullyConstrained = false
  MakeInternals = false
  MapMode = 5
  Placement = pos=(151.904,-47,8.59107) rot=(0,-1,0;0.14677rad)
  sketch-geometry (14):
    g0: LineSegment StartX=-2.25 StartY=22.5 StartZ=0 EndX=-2.25 EndY=-22.5 EndZ=0
    g1: LineSegment StartX=-2.25 StartY=-22.5 StartZ=0 EndX=-5.25 EndY=-22.5 EndZ=0
    g2: LineSegment StartX=-5.25 StartY=-22.5 StartZ=0 EndX=-5.25 EndY=22.5 EndZ=0
    g3: LineSegment StartX=-5.25 StartY=22.5 StartZ=0 EndX=-2.25 EndY=22.5 EndZ=0
    g4: LineSegment StartX=-143.345 StartY=-20.1 StartZ=0 EndX=-143.345 EndY=-40.1 EndZ=0
    g5: LineSegment StartX=-143.345 StartY=-40.1 StartZ=0 EndX=-140.345 EndY=-40.1 EndZ=0
    g6: LineSegment StartX=-140.345 StartY=-40.1 StartZ=0 EndX=-140.345 EndY=-20.1 EndZ=0
    g7: LineSegment StartX=-140.345 StartY=-20.1 StartZ=0 EndX=-143.345 EndY=-20.1 EndZ=0
    g8: LineSegment StartX=-140.345 StartY=40.1 StartZ=0 EndX=-140.345 EndY=20.1 EndZ=0
    g9: LineSegment StartX=-140.345 StartY=20.1 StartZ=0 EndX=-143.345 EndY=20.1 EndZ=0
    g10: LineSegment StartX=-143.345 StartY=20.1 StartZ=0 EndX=-143.345 EndY=40.1 EndZ=0
    g11: LineSegment StartX=-143.345 StartY=40.1 StartZ=0 EndX=-140.345 EndY=40.1 EndZ=0
    g12: GeomPoint [constr] X=-123.414 Y=203.004 Z=0
    g13: GeomPoint [constr] X=-123.414 Y=-201.75 Z=0
  constraints (34):
    c: Coincident(g0,g1)
    c: Coincident(g1,g2)
    c: Coincident(g2,g3)
    c: Coincident(g3,g0)
    c: Horizontal(g1)
    c: Horizontal(g3)
    c: Vertical(g0)
    c: Coincident(g4,g5)
    c: Coincident(g5,g6)
    c: Coincident(g6,g7)
    c: Coincident(g7,g4)
    c: Horizontal(g5)
    c: Horizontal(g7)
    c: Vertical(g4)
    c: Vertical(g6)
    c: Coincident(g8,g9)
    c: Coincident(g9,g10)
    c: Coincident(g10,g11)
    c: Coincident(g11,g8)
    c: Horizontal(g9)
    c: Horizontal(g11)
    c: Vertical(g8)
    c: Vertical(g10)
    c: DistanceY(g4,g4) = 20
    c: Symmetric(g6,g8,g-1)
    c: Equal(g10,g4)
    c: Symmetric(g2,g1,g-1)
    c: Equal(g11,g3)
    c: DistanceX(g0,g-1) = 2.25
    c: Distance(g3,g3) = 3
    c: DistanceY(g2,g2) = 45
    c: Vertical(g9,g4)
    c: DistanceY(g10,g-3) = 3
    c: DistanceX(g-3,g10) = 2
FEATURE [PartDesign::Plane] DatumPlane015  label="Front section plane"
  AttachmentOffset = pos=(0,0,-7.5) rot=(0,0,1;0rad)
  AttachmentSupport = -> [Pad004]
  Length = 137.592
  MapMode = 5
  Placement = pos=(148.5,0,0) rot=(0.57735,0.57735,0.57735;2.0944rad)
  ResizeMode = 0
  Width = 81.1837
FEATURE [Sketcher::SketchObject] Sketch024  label="ConstructionSketch"
  ArcFitTolerance = 0
  AttachmentSupport = -> [DatumPlane015]
  FullyConstrained = false
  MakeInternals = false
  MapMode = 5
  Placement = pos=(148.5,0,0) rot=(0.57735,0.57735,0.57735;2.0944rad)
  sketch-geometry (2):
    g0: LineSegment StartX=-94.4939 StartY=31.3405 StartZ=0 EndX=-94.4939 EndY=-17.3848 EndZ=0
    g1: LineSegment StartX=17.1406 StartY=31.6743 StartZ=0 EndX=17.1406 EndY=-24.8939 EndZ=0
  constraints (2):
    c: Vertical(g0)
    c: Vertical(g1)
FEATURE [PartDesign::Point] DatumPoint004
  AttacherType = Attacher::AttachEnginePoint
  AttachmentSupport = -> [DatumPlane012,Sketch024]
  MapMode = 40
  Placement = pos=(148.5,-94.4939,11.8767) rot=(0,0,1;0rad)
FEATURE [PartDesign::Point] DatumPoint005
  AttacherType = Attacher::AttachEnginePoint
  AttachmentSupport = -> [Sketch024,DatumPlane012]
  MapMode = 40
  Placement = pos=(148.5,17.1406,11.8767) rot=(0,0,1;0rad)
FEATURE [PartDesign::Line] DatumLine007  label="Front plane intersection with top of PCB"
  AttacherType = Attacher::AttachEngineLine
  AttachmentSupport = -> [DatumPoint005,DatumPoint004]
  Length = 20
  MapMode = 29
  Placement = pos=(148.5,17.1406,11.8767) rot=(1,0,0;1.5708rad)
  ResizeMode = 0
FEATURE [Sketcher::SketchObject] Sketch025  label="Front section"
  ArcFitTolerance = 0
  AttachmentSupport = -> [DatumPlane015]
  ExternalGeometry = -> [DatumPlane014,Pad004]
  FullyConstrained = true
  MakeInternals = false
  MapMode = 5
  Placement = pos=(148.5,0,0) rot=(0.57735,0.57735,0.57735;2.0944rad)
  sketch-geometry (12):
    g0: LineSegment StartX=-89.6 StartY=65.2228 StartZ=0 EndX=-4.4 EndY=65.2228 EndZ=0
    g1: LineSegment StartX=-4.4 StartY=65.2228 StartZ=0 EndX=-4.4 EndY=14.2728 EndZ=0
    g2: LineSegment StartX=-4.4 StartY=14.2728 StartZ=0 EndX=-6.4 EndY=14.2728 EndZ=0
    g3: LineSegment StartX=-6.4 StartY=14.2728 StartZ=0 EndX=-6.4 EndY=10.2728 EndZ=0
    g4: LineSegment StartX=-6.4 StartY=10.2728 StartZ=0 EndX=-8.9 EndY=10.2728 EndZ=0
    g5: LineSegment StartX=-8.9 StartY=10.2728 StartZ=0 EndX=-8.9 EndY=10.2528 EndZ=0
    g6: LineSegment StartX=-8.9 StartY=10.2528 StartZ=0 EndX=-85.1 EndY=10.2528 EndZ=0
    g7: LineSegment StartX=-85.1 StartY=10.2528 StartZ=0 EndX=-85.1 EndY=10.2728 EndZ=0
    g8: LineSegment StartX=-85.1 StartY=10.2728 StartZ=0 EndX=-87.6 EndY=10.2728 EndZ=0
    g9: LineSegment StartX=-87.6 StartY=10.2728 StartZ=0 EndX=-87.6 EndY=14.2728 EndZ=0
    g10: LineSegment StartX=-87.6 StartY=14.2728 StartZ=0 EndX=-89.6 EndY=14.2728 EndZ=0
    g11: LineSegment StartX=-89.6 StartY=14.2728 StartZ=0 EndX=-89.6 EndY=65.2228 EndZ=0
  constraints (35):
    c: Vertical(g1)
    c: Coincident(g1,g2)
    c: Horizontal(g2)
    c: Coincident(g2,g3)
    c: Vertical(g3)
    c: Coincident(g3,g4)
    c: Horizontal(g4)
    c: Coincident(g4,g5)
    c: Vertical(g5)
    c: Coincident(g5,g6)
    c: Horizontal(g6)
    c: Coincident(g6,g7)
    c: Vertical(g7)
    c: Coincident(g7,g8)
    c: Horizontal(g8)
    c: Coincident(g8,g9)
    c: Vertical(g9)
    c: Coincident(g9,g10)
    c: Horizontal(g10)
    c: Coincident(g10,g11)
    c: Coincident(g11,g0)
    c: Vertical(g11)
    c: Horizontal(g9,g2)
    c: Horizontal(g7,g4)
    c: Equal(g10,g2)
    c: Equal(g8,g4)
    c: Symmetric(g0,g0,g-3)
    c: DistanceX(g10,g10) = 2
    c: DistanceX(g8,g8) = 2.5
    c: DistanceY(g7,g7) = 0.02
    c: DistanceX(g-4,g0) = 5.5
    c: DistanceY(g-4,g1) = 50
    c: Coincident(g0,g1)
    c: DistanceY(g8,g-4) = 4.95
    c: DistanceY(g3,g3) = 4
FEATURE [Sketcher::SketchObject] Sketch021  label="BackSection"
  ArcFitTolerance = 0
  AttachmentOffset = pos=(0,0,11) rot=(0,0,1;0rad)
  AttachmentSupport = -> [YZ_Plane004]
  ExternalGeometry = -> [Pad005,Sketch025]
  FullyConstrained = false
  MakeInternals = false
  MapMode = 5
  Placement = pos=(11,0,0) rot=(0.57735,0.57735,0.57735;2.0944rad)
  sketch-geometry (15):
    g0: LineSegment StartX=-6.5 StartY=10.2728 StartZ=0 EndX=-87.5 EndY=10.2728 EndZ=0
    g1: LineSegment StartX=-89.6 StartY=38.6916 StartZ=0 EndX=-4.4 EndY=38.6916 EndZ=0
    g2: LineSegment StartX=-89.6 StartY=38.1916 StartZ=0 EndX=-89.6 EndY=38.6916 EndZ=0
    g3: LineSegment StartX=-87.6 StartY=38.1916 StartZ=0 EndX=-89.6 EndY=38.1916 EndZ=0
    g4: LineSegment StartX=-87.6 StartY=36.5916 StartZ=0 EndX=-87.6 EndY=38.1916 EndZ=0
    g5: LineSegment StartX=-4.4 StartY=38.6916 StartZ=0 EndX=-4.4 EndY=38.1916 EndZ=0
    g6: LineSegment StartX=-4.4 StartY=38.1916 StartZ=0 EndX=-6.4 EndY=38.1916 EndZ=0
    g7: LineSegment StartX=-6.4 StartY=38.1916 StartZ=0 EndX=-6.4 EndY=36.5916 EndZ=0
    g8: LineSegment StartX=-87.5 StartY=10.2728 StartZ=0 EndX=-87.5 EndY=36.5916 EndZ=0
    g9: LineSegment StartX=-87.5 StartY=36.5916 StartZ=0 EndX=-87.6 EndY=36.5916 EndZ=0
    g10: LineSegment StartX=-6.4 StartY=36.5916 StartZ=0 EndX=-6.5 EndY=36.5916 EndZ=0
    g11: LineSegment StartX=-6.5 StartY=36.5916 StartZ=0 EndX=-6.5 EndY=10.2728 EndZ=0
    g12: GeomPoint [constr] X=-47 Y=38.6916 Z=0
    g13: GeomPoint [constr] X=-47 Y=8.45 Z=0
    g14: LineSegment [constr] StartX=-47 StartY=38.6916 StartZ=0 EndX=-47 EndY=8.51688 EndZ=0
  constraints (37):
    c: Coincident(g0,g8)
    c: Coincident(g2,g1)
    c: Coincident(g1,g5)
    c: Coincident(g11,g0)
    c: Horizontal(g0)
    c: PointOnObject(g2,g-6)
    c: Coincident(g3,g2)
    c: Vertical(g2)
    c: Coincident(g4,g3)
    c: Coincident(g9,g4)
    c: Vertical(g4)
    c: Coincident(g5,g6)
    c: Vertical(g5)
    c: Coincident(g6,g7)
    c: Coincident(g7,g10)
    c: Vertical(g7)
    c: Coincident(g8,g9)
    c: Vertical(g8)
    c: Coincident(g10,g11)
    c: Vertical(g11)
    c: Horizontal(g3)
    c: Horizontal(g6)
    c: Horizontal(g9)
    c: Horizontal(g10)
    c: Horizontal(g8,g10)
    c: Symmetric(g-6,g-6,g12)
    c: Symmetric(g-4,g-5,g13)
    c: Coincident(g14,g12)
    c: Symmetric(g1,g1,g14)
    c: Symmetric(g3,g6,g14)
    c: Symmetric(g0,g0,g14)
    c: Vertical(g2,g-7)
    c: DistanceX(g3,g3) = 2
    c: DistanceX(g9,g9) = 0.1
    c: DistanceY(g4,g4) = 1.6
    c: Horizontal(g-8,g0)
    c: DistanceY(g5,g5) = 0.5
FEATURE [Sketcher::SketchObject] Sketch022  label="MiddleSection"
  ArcFitTolerance = 0
  AttachmentSupport = -> [Pad005]
  ExternalGeometry = -> [Sketch021,Pad005]
  FullyConstrained = true
  MakeInternals = false
  MapMode = 5
  Placement = pos=(35,-5.37e-14,2.02e-14) rot=(0.57735,0.57735,-0.57735;4.18879rad)
  sketch-geometry (12):
    g0: LineSegment StartX=-89.35 StartY=-38.6916 StartZ=0 EndX=-4.65 EndY=-38.6916 EndZ=0
    g1: LineSegment StartX=-4.65 StartY=-38.6916 StartZ=0 EndX=-4.65 EndY=-35.9916 EndZ=0
    g2: LineSegment StartX=-4.65 StartY=-35.9916 StartZ=0 EndX=-6.65 EndY=-35.9916 EndZ=0
    g3: LineSegment StartX=-6.75 StartY=-10.2728 StartZ=0 EndX=-87.25 EndY=-10.2728 EndZ=0
    g4: LineSegment StartX=-87.35 StartY=-35.9916 StartZ=0 EndX=-89.35 EndY=-35.9916 EndZ=0
    g5: LineSegment StartX=-89.35 StartY=-35.9916 StartZ=0 EndX=-89.35 EndY=-38.6916 EndZ=0
    g6: LineSegment StartX=-87.25 StartY=-10.2728 StartZ=0 EndX=-87.25 EndY=-31.9916 EndZ=0
    g7: LineSegment StartX=-6.75 StartY=-31.9916 StartZ=0 EndX=-6.75 EndY=-10.2728 EndZ=0
    g8: LineSegment StartX=-6.65 StartY=-35.9916 StartZ=0 EndX=-6.65 EndY=-31.9916 EndZ=0
    g9: LineSegment StartX=-6.65 StartY=-31.9916 StartZ=0 EndX=-6.75 EndY=-31.9916 EndZ=0
    g10: LineSegment StartX=-87.25 StartY=-31.9916 StartZ=0 EndX=-87.35 EndY=-31.9916 EndZ=0
    g11: LineSegment StartX=-87.35 StartY=-31.9916 StartZ=0 EndX=-87.35 EndY=-35.9916 EndZ=0
  constraints (36):
    c: PointOnObject(g0,g-4)
    c: PointOnObject(g0,g-4)
    c: Coincident(g0,g1)
    c: Coincident(g1,g2)
    c: Coincident(g2,g8)
    c: Coincident(g11,g4)
    c: Coincident(g4,g5)
    c: Coincident(g5,g0)
    c: Vertical(g5)
    c: Vertical(g1)
    c: Horizontal(g4,g1)
    c: DistanceX(g-4,g0) = 2
    c: DistanceX(g0,g-4) = 2
    c: Horizontal(g4)
    c: Horizontal(g2)
    c: DistanceX(g2,g1) = 2
    c: Equal(g4,g2)
    c: Coincident(g6,g10)
    c: Coincident(g9,g7)
    c: Coincident(g3,g7)
    c: PointOnObject(g3,g-3)
    c: Vertical(g7)
    c: Coincident(g8,g9)
    c: Coincident(g10,g11)
    c: Coincident(g6,g3)
    c: PointOnObject(g3,g-3)
    c: Vertical(g6)
    c: Horizontal(g9)
    c: Horizontal(g10)
    c: Horizontal(g6,g7)
    c: Vertical(g11)
    c: Vertical(g8)
    c: Equal(g10,g9)
    c: DistanceX(g10,g10) = 0.1
    c: DistanceY(g0,g10) = 6.7
    c: DistanceY(g11,g11) = 4
FEATURE [Sketcher::SketchObject] Sketch038  label="Tranche 2.2"
  ArcFitTolerance = 1e-06
  AttachmentOffset = pos=(0,0,-20) rot=(0,0,1;0rad)
  AttachmentSupport = -> [Pad005]
  FullyConstrained = true
  MakeInternals = false
  MapMode = 5
  Placement = pos=(55,-5.37e-14,2.02e-14) rot=(0.57735,0.57735,-0.57735;4.18879rad)
  expr: Constraints[32] = 21.72 - 20 * sin(11)
  sketch-geometry (12):
    g0: LineSegment StartX=-89.6 StartY=-38.1738 StartZ=0 EndX=-4.4 EndY=-38.1738 EndZ=0
    g1: LineSegment StartX=-4.4 StartY=-38.1738 StartZ=0 EndX=-4.4 EndY=-32.1738 EndZ=0
    g2: LineSegment StartX=-4.4 StartY=-32.1738 StartZ=0 EndX=-6.4 EndY=-32.1738 EndZ=0
    g3: LineSegment StartX=-8.9 StartY=-10.27 StartZ=0 EndX=-85.1 EndY=-10.27 EndZ=0
    g4: LineSegment StartX=-87.6 StartY=-32.1738 StartZ=0 EndX=-89.6 EndY=-32.1738 EndZ=0
    g5: LineSegment StartX=-89.6 StartY=-32.1738 StartZ=0 EndX=-89.6 EndY=-38.1738 EndZ=0
    g6: LineSegment StartX=-85.1 StartY=-10.27 StartZ=0 EndX=-85.1 EndY=-28.1738 EndZ=0
    g7: LineSegment StartX=-8.9 StartY=-28.1738 StartZ=0 EndX=-8.9 EndY=-10.27 EndZ=0
    g8: LineSegment StartX=-6.4 StartY=-32.1738 StartZ=0 EndX=-6.4 EndY=-28.1738 EndZ=0
    g9: LineSegment StartX=-6.4 StartY=-28.1738 StartZ=0 EndX=-8.9 EndY=-28.1738 EndZ=0
    g10: LineSegment StartX=-85.1 StartY=-28.1738 StartZ=0 EndX=-87.6 EndY=-28.1738 EndZ=0
    g11: LineSegment StartX=-87.6 StartY=-28.1738 StartZ=0 EndX=-87.6 EndY=-32.1738 EndZ=0
  constraints (36):
    c: Coincident(g0,g1)
    c: Coincident(g1,g2)
    c: Coincident(g2,g8)
    c: Coincident(g11,g4)
    c: Coincident(g4,g5)
    c: Coincident(g5,g0)
    c: Vertical(g5)
    c: Vertical(g1)
    c: Horizontal(g4,g1)
    c: Horizontal(g4)
    c: Horizontal(g2)
    c: DistanceX(g2,g1) = 2
    c: Equal(g4,g2)
    c: Coincident(g6,g10)
    c: Coincident(g9,g7)
    c: Coincident(g3,g7)
    c: Vertical(g7)
    c: Coincident(g8,g9)
    c: Coincident(g10,g11)
    c: Coincident(g6,g3)
    c: Vertical(g6)
    c: Horizontal(g9)
    c: Horizontal(g10)
    c: Horizontal(g6,g7)
    c: Vertical(g11)
    c: Vertical(g8)
    c: Equal(g10,g9)
    c: DistanceX(g10,g10) = 2.5
    c: DistanceY(g0,g10) = 10
    c: DistanceY(g11,g11) = 4
    c: DistanceY(g3,g-1) = 10.27
    c: DistanceX(g3,g-1) = 8.9
    c: DistanceY(g7,g7) = 17.9038
    c: Horizontal(g0)
    c: DistanceX(g0,g0) = 85.2
    c: Horizontal(g3)
FEATURE [Sketcher::SketchObject] Sketch039  label="Tranche 2.1"
  ArcFitTolerance = 1e-06
  AttachmentOffset = pos=(0,0,-15) rot=(0,0,1;0rad)
  AttachmentSupport = -> [Pad005]
  ExternalGeometry = -> [Sketch038]
  FullyConstrained = true
  MakeInternals = false
  MapMode = 5
  Placement = pos=(50,-5.37e-14,2.02e-14) rot=(0.57735,0.57735,-0.57735;4.18879rad)
  expr: Constraints[34] = 5 * sin(11)
  expr: Constraints[35] = 5 * sin(11)
  sketch-geometry (12):
    g0: LineSegment StartX=-89.6 StartY=-38.1738 StartZ=0 EndX=-89.6 EndY=-33.1279 EndZ=0
    g1: LineSegment StartX=-89.6 StartY=-33.1279 StartZ=0 EndX=-87.6 EndY=-33.1279 EndZ=0
    g2: LineSegment StartX=-87.6 StartY=-33.1279 StartZ=0 EndX=-87.6 EndY=-29.1279 EndZ=0
    g3: LineSegment StartX=-87.6 StartY=-29.1279 StartZ=0 EndX=-87.5 EndY=-29.1279 EndZ=0
    g4: LineSegment StartX=-87.5 StartY=-29.1279 StartZ=0 EndX=-87.5 EndY=-10.27 EndZ=0
    g5: LineSegment StartX=-87.5 StartY=-10.27 StartZ=0 EndX=-6.5 EndY=-10.27 EndZ=0
    g6: LineSegment StartX=-6.5 StartY=-10.27 StartZ=0 EndX=-6.5 EndY=-29.1279 EndZ=0
    g7: LineSegment StartX=-6.5 StartY=-29.1279 StartZ=0 EndX=-6.4 EndY=-29.1279 EndZ=0
    g8: LineSegment StartX=-6.4 StartY=-29.1279 StartZ=0 EndX=-6.4 EndY=-33.1279 EndZ=0
    g9: LineSegment StartX=-6.4 StartY=-33.1279 StartZ=0 EndX=-4.4 EndY=-33.1279 EndZ=0
    g10: LineSegment StartX=-4.4 StartY=-33.1279 StartZ=0 EndX=-4.4 EndY=-38.1738 EndZ=0
    g11: LineSegment StartX=-4.4 StartY=-38.1738 StartZ=0 EndX=-89.6 EndY=-38.1738 EndZ=0
  constraints (36):
    c: Vertical(g0)
    c: Coincident(g0,g1)
    c: Horizontal(g1)
    c: Coincident(g1,g2)
    c: Vertical(g2)
    c: Coincident(g2,g3)
    c: Horizontal(g3)
    c: Coincident(g3,g4)
    c: Vertical(g4)
    c: Coincident(g4,g5)
    c: Horizontal(g5)
    c: Coincident(g5,g6)
    c: Vertical(g6)
    c: Coincident(g6,g7)
    c: Horizontal(g7)
    c: Coincident(g7,g8)
    c: Vertical(g8)
    c: Coincident(g8,g9)
    c: Horizontal(g9)
    c: Coincident(g9,g10)
    c: Vertical(g10)
    c: Coincident(g10,g11)
    c: Coincident(g11,g0)
    c: Horizontal(g11)
    c: Horizontal(g8,g1)
    c: Horizontal(g4,g-10)
    c: PointOnObject(g-3,g0)
    c: PointOnObject(g-4,g10)
    c: DistanceX(g3,g3) = 0.1
    c: DistanceX(g7,g7) = 0.1
    c: Horizontal(g3,g6)
    c: PointOnObject(g-13,g2)
    c: PointOnObject(g-6,g8)
    c: PointOnObject(g-3,g11)
    c: DistanceY(g3,g-11) = 0.954045
    c: DistanceY(g1,g-13) = 0.954045
FEATURE [PartDesign::SubtractiveLoft] SubtractiveLoft
  BaseFeature = -> Pad007
  Closed = false
  Placement = pos=(156,0,0) rot=(0.57735,0.57735,0.57735;2.0944rad)
  Profile = -> Sketch021
  Refine = true
  Ruled = true
  Sections = -> [Sketch022,Sketch039,Sketch038,Sketch025]
  Suppressed = false
FEATURE [Sketcher::SketchObject] Sketch026  label="PCB support sketch001"
  ArcFitTolerance = 0
  AttachmentSupport = -> [SubtractiveLoft]
  ExternalGeometry = -> [SubtractiveLoft]
  FullyConstrained = true
  MakeInternals = false
  MapMode = 5
  Placement = pos=(156.002,-2.3e-15,10.2515) rot=(-9.2e-05,9.2e-05,-1;1.5708rad)
  sketch-geometry (5):
    g0: Circle CenterX=28.9 CenterY=-87.5019 CenterZ=0 NormalX=0 NormalY=0 NormalZ=1 AngleXU=0 Radius=2.5
    g1: Circle CenterX=28.9 CenterY=-50.0019 CenterZ=0 NormalX=0 NormalY=0 NormalZ=1 AngleXU=0 Radius=2.5
    g2: Circle CenterX=65.1 CenterY=-50.0019 CenterZ=0 NormalX=0 NormalY=0 NormalZ=1 AngleXU=0 Radius=2.5
    g3: Circle CenterX=65.1 CenterY=-87.5019 CenterZ=0 NormalX=0 NormalY=0 NormalZ=1 AngleXU=0 Radius=2.5
    g4: Circle CenterX=47 CenterY=-68.7519 CenterZ=0 NormalX=0 NormalY=0 NormalZ=1 AngleXU=0 Radius=2.5
  constraints (14):
    c: Diameter(g0) = 5
    c: Equal(g1,g0)
    c: Vertical(g1,g0)
    c: Equal(g0,g4)
    c: Equal(g0,g2)
    c: Equal(g0,g3)
    c: Horizontal(g0,g3)
    c: Horizontal(g1,g2)
    c: Vertical(g2,g3)
    c: Symmetric(g0,g2,g4)
    c: DistanceY(g1,g-4) = 42.5
    c: DistanceY(g0,g-4) = 80
    c: DistanceX(g-4,g1) = 20
    c: DistanceX(g2,g-3) = 20
FEATURE [PartDesign::Pad] Pad008  label="PCB support"
  BaseFeature = -> SubtractiveLoft
  Direction = (0.000183572,0,1)
  Length = 10
  Length2 = 10
  Placement = pos=(156,0,0) rot=(0.57735,0.57735,0.57735;2.0944rad)
  Profile = -> Sketch026
  ReferenceAxis = -> Sketch026 [N_Axis]
  Refine = true
  Suppressed = false
  Type = 3
  UpToFace = -> SubtractiveLoft [Face38]
FEATURE [PartDesign::Pocket] Pocket006  label="Joystick ports"
  BaseFeature = -> Pad008
  Direction = (0,1,-2e-16)
  Length = 5
  Length2 = 5
  Midplane = true
  Placement = pos=(156,0,0) rot=(0.57735,0.57735,0.57735;2.0944rad)
  Profile = -> Sketch027
  ReferenceAxis = -> Sketch027 [N_Axis]
  Suppressed = false
  Type = 1
FEATURE [Sketcher::SketchObject] Sketch028  label="Boot select access sketch"
  ArcFitTolerance = 0
  AttachmentSupport = -> [Pocket006]
  ExternalGeometry = -> [Pocket006]
  FullyConstrained = true
  MakeInternals = false
  MapMode = 5
  Placement = pos=(156,-8.4e-15,8.45) rot=(0.707107,0.707107,0;3.14159rad)
  sketch-geometry (9):
    g0: LineSegment StartX=-88.1 StartY=-12.5 StartZ=0 EndX=-83.1 EndY=-12.5 EndZ=0
    g1: ArcOfCircle CenterX=-83.1 CenterY=-14.5 CenterZ=0 NormalX=0 NormalY=0 NormalZ=1 AngleXU=0 Radius=2 StartAngle=1.959e-13 EndAngle=1.5708
    g2: LineSegment StartX=-81.1 StartY=-14.5 StartZ=0 EndX=-81.1 EndY=-20.5 EndZ=0
    g3: ArcOfCircle CenterX=-83.1 CenterY=-20.5 CenterZ=0 NormalX=0 NormalY=0 NormalZ=1 AngleXU=0 Radius=2 StartAngle=4.71239 EndAngle=6.28319
    g4: LineSegment StartX=-83.1 StartY=-22.5 StartZ=0 EndX=-88.1 EndY=-22.5 EndZ=0
    g5: LineSegment StartX=-90.1 StartY=-24.5 StartZ=0 EndX=-90.1 EndY=-10.5 EndZ=0
    g6: ArcOfCircle CenterX=-88.1 CenterY=-24.5 CenterZ=0 NormalX=0 NormalY=0 NormalZ=1 AngleXU=0 Radius=2 StartAngle=1.5708 EndAngle=3.14159
    g7: ArcOfCircle CenterX=-88.1 CenterY=-10.5 CenterZ=0 NormalX=0 NormalY=0 NormalZ=1 AngleXU=0 Radius=2 StartAngle=3.14159 EndAngle=4.71239
    g8: GeomPoint X=-81.1 Y=-17.5 Z=0
  constraints (25):
    c: Tangent(g0,g1) = 1.5708
    c: Tangent(g1,g2) = 1.5708
    c: Tangent(g2,g3) = 1.5708
    c: Tangent(g3,g4) = 1.5708
    c: Horizontal(g0)
    c: Horizontal(g4)
    c: Vertical(g2)
    c: Vertical(g5)
    c: Equal(g1,g3)
    c: DistanceY(g3,g0) = 10
    c: DistanceX(g5,g1) = 9
    c: Coincident(g6,g4)
    c: Coincident(g7,g0)
    c: Vertical(g7,g0)
    c: Horizontal(g7,g7)
    c: Radius(g7) = 2
    c: Equal(g7,g6)
    c: Equal(g7,g1)
    c: Horizontal(g6,g6)
    c: Vertical(g4,g6)
    c: Coincident(g5,g6)
    c: Coincident(g5,g7)
    c: Symmetric(g2,g2,g8)
    c: DistanceY(g8,g-4) = 10
    c: PointOnObject(g5,g-3)
FEATURE [PartDesign::Pocket] Pocket007  label="Boot select access"
  BaseFeature = -> Pocket006
  Direction = (1.3e-15,0,1)
  Length = 0
  Length2 = 5
  Placement = pos=(156,0,0) rot=(0.57735,0.57735,0.57735;2.0944rad)
  Profile = -> Sketch028
  ReferenceAxis = -> Sketch028 [N_Axis]
  Suppressed = false
  Type = 3
  UpToFace = -> Pocket006 [Face38]
FEATURE [Sketcher::SketchObject] Sketch029  label="Bottom screw holes sketch"
  ArcFitTolerance = 0
  AttachmentSupport = -> [Pocket007]
  ExternalGeometry = -> [Binder015]
  FullyConstrained = true
  MakeInternals = false
  MapMode = 5
  Placement = pos=(158.846,-9.1e-15,14.6709) rot=(-0.095208,0.095208,-0.990894;1.57994rad)
  sketch-geometry (2):
    g0: Circle CenterX=18.9 CenterY=-6.39856 CenterZ=0 NormalX=0 NormalY=0 NormalZ=1 AngleXU=0 Radius=1.5
    g1: Circle CenterX=75.1 CenterY=-6.39856 CenterZ=0 NormalX=0 NormalY=0 NormalZ=1 AngleXU=0 Radius=1.5
  constraints (4):
    c: Coincident(g0,g-3)
    c: Coincident(g1,g-4)
    c: Equal(g-3,g0)
    c: Equal(g1,g-4)
FEATURE [PartDesign::Fillet] Fillet001  label="Bottom fillet"
  Base = -> Pocket007 [Edge25,Edge32,Edge24]
  BaseFeature = -> Pocket007
  Placement = pos=(156,0,0) rot=(0.57735,0.57735,0.57735;2.0944rad)
  Radius = 1
  SupportTransform = false
  Suppressed = false
  UseAllEdges = false
FEATURE [Sketcher::SketchObject] Sketch032  label="right port sketch"
  ArcFitTolerance = 0
  AttachmentSupport = -> [Fillet001]
  ExternalGeometry = -> [Clone2D001]
  FullyConstrained = true
  MakeInternals = false
  MapMode = 45
  Placement = pos=(69.634,-3.9,15.2731) rot=(-0.590996,-0.570405,-0.570405;2.07405rad)
  sketch-geometry (8):
    g0: LineSegment StartX=14.2466 StartY=-24.1572 StartZ=0 EndX=17.5203 EndY=-44.9004 EndZ=0
    g1: ArcOfCircle CenterX=15.5448 CenterY=-45.2122 CenterZ=0 NormalX=0 NormalY=0 NormalZ=1 AngleXU=0 Radius=2 StartAngle=4.86892 EndAngle=6.43972
    g2: LineSegment StartX=15.8566 StartY=-47.1878 StartZ=0 EndX=6.96659 EndY=-48.5908 EndZ=0
    g3: ArcOfCircle CenterX=6.6548 CenterY=-46.6152 CenterZ=0 NormalX=0 NormalY=0 NormalZ=1 AngleXU=0 Radius=2 StartAngle=3.29812 EndAngle=4.86892
    g4: LineSegment StartX=4.67926 StartY=-46.927 StartZ=0 EndX=1.40553 EndY=-26.1838 EndZ=0
    g5: ArcOfCircle CenterX=3.38108 CenterY=-25.872 CenterZ=0 NormalX=0 NormalY=0 NormalZ=1 AngleXU=0 Radius=2 StartAngle=1.72733 EndAngle=3.29812
    g6: ArcOfCircle CenterX=12.271 CenterY=-24.469 CenterZ=0 NormalX=0 NormalY=0 NormalZ=1 AngleXU=0 Radius=2 StartAngle=0.15653 EndAngle=1.72733
    g7: LineSegment StartX=3.0693 StartY=-23.8964 StartZ=0 EndX=11.9593 EndY=-22.4934 EndZ=0
  constraints (16):
    c: Coincident(g0,g-5)
    c: Tangent(g0,g1) = 1.5708
    c: Coincident(g1,g-6)
    c: Coincident(g1,g2)
    c: Coincident(g2,g-7)
    c: Tangent(g2,g3) = 1.5708
    c: Coincident(g3,g-8)
    c: Coincident(g3,g4)
    c: Coincident(g4,g-8)
    c: Coincident(g0,g-4)
    c: Coincident(g5,g4)
    c: Coincident(g6,g0)
    c: Coincident(g5,g-9)
    c: Coincident(g6,g-9)
    c: Tangent(g7,g5) = 1.5708
    c: Tangent(g7,g6) = 1.5708
FEATURE [PartDesign::Pocket] Pocket009  label="Right port"
  BaseFeature = -> Fillet001
  Direction = (2.9e-15,-1,-1.3e-15)
  Length = 5
  Length2 = 5
  Placement = pos=(156,0,0) rot=(0.57735,0.57735,0.57735;2.0944rad)
  Profile = -> Sketch032
  ReferenceAxis = -> Sketch032 [N_Axis]
  Refine = true
  Reversed = true
  Suppressed = false
  Type = 1
FEATURE [Sketcher::SketchObject] Sketch033
  ArcFitTolerance = 0
  AttachmentSupport = -> [Pocket006]
  ExternalGeometry = -> [Sketch032]
  FullyConstrained = true
  MakeInternals = false
  MapMode = 45
  Placement = pos=(69.634,-90.1,15.2731) rot=(-0.590996,-0.570405,-0.570405;2.07405rad)
  sketch-geometry (8):
    g0: LineSegment StartX=3.0693 StartY=-23.8964 StartZ=0 EndX=11.9593 EndY=-22.4934 EndZ=0
    g1: ArcOfCircle CenterX=12.271 CenterY=-24.469 CenterZ=0 NormalX=0 NormalY=0 NormalZ=1 AngleXU=0 Radius=2 StartAngle=0.15653 EndAngle=1.72733
    g2: LineSegment StartX=14.2466 StartY=-24.1572 StartZ=0 EndX=17.5203 EndY=-44.9004 EndZ=0
    g3: ArcOfCircle CenterX=15.5448 CenterY=-45.2122 CenterZ=0 NormalX=0 NormalY=0 NormalZ=1 AngleXU=0 Radius=2 StartAngle=4.86892 EndAngle=6.43972
    g4: LineSegment StartX=15.8566 StartY=-47.1878 StartZ=0 EndX=6.96659 EndY=-48.5908 EndZ=0
    g5: ArcOfCircle CenterX=6.65481 CenterY=-46.6152 CenterZ=0 NormalX=0 NormalY=0 NormalZ=1 AngleXU=0 Radius=2 StartAngle=3.29812 EndAngle=4.86892
    g6: LineSegment StartX=4.67926 StartY=-46.927 StartZ=0 EndX=1.40553 EndY=-26.1838 EndZ=0
    g7: ArcOfCircle CenterX=3.38108 CenterY=-25.872 CenterZ=0 NormalX=0 NormalY=0 NormalZ=1 AngleXU=0 Radius=2 StartAngle=1.72733 EndAngle=3.29812
  constraints (16):
    c: Coincident(g-3,g0)
    c: Coincident(g0,g-4)
    c: Tangent(g0,g1) = 1.5708
    c: Coincident(g1,g-4)
    c: Coincident(g1,g2)
    c: Coincident(g2,g-5)
    c: Tangent(g2,g3) = 1.5708
    c: Coincident(g3,g-5)
    c: Coincident(g3,g4)
    c: Coincident(g4,g-6)
    c: Tangent(g4,g5) = 1.5708
    c: Coincident(g5,g-6)
    c: Coincident(g5,g6)
    c: Coincident(g6,g-3)
    c: Tangent(g6,g7) = 1.5708
    c: Coincident(g7,g0)
FEATURE [PartDesign::Pocket] Pocket010  label="Left port"
  BaseFeature = -> Pocket009
  Direction = (2.1e-15,-1,-1.69e-14)
  Length = 5
  Length2 = 5
  Placement = pos=(156,0,0) rot=(0.57735,0.57735,0.57735;2.0944rad)
  Profile = -> Sketch033
  ReferenceAxis = -> Sketch033 [N_Axis]
  Refine = true
  Suppressed = false
  Type = 1
FEATURE [PartDesign::Pocket] Pocket011  label="Bottom screw holes"
  BaseFeature = -> Pocket010
  Direction = (-0.190408,0,-0.981705)
  Length = 5
  Length2 = 5
  Placement = pos=(156,0,0) rot=(0.57735,0.57735,0.57735;2.0944rad)
  Profile = -> Sketch029
  ReferenceAxis = -> Sketch029 [N_Axis]
  Suppressed = false
  Type = 1
FEATURE [PartDesign::Pad] Pad009  label="Alignment pegs"
  BaseFeature = -> Pocket011
  Direction = (0.190408,0,0.981705)
  Length = 1.2
  Length2 = 10
  Placement = pos=(156,0,0) rot=(0.57735,0.57735,0.57735;2.0944rad)
  Profile = -> Sketch030
  ReferenceAxis = -> Sketch030 [N_Axis]
  Suppressed = false
  Type = 0
FEATURE [PartDesign::Chamfer] Chamfer
  Angle = 45
  Base = -> Pad009 [Edge114,Edge116,Edge124,Edge112,Edge118,Edge106,Edge104,Edge102]
  BaseFeature = -> Pad009
  ChamferType = 0
  FlipDirection = false
  Placement = pos=(156,0,0) rot=(0.57735,0.57735,0.57735;2.0944rad)
  Size = 0.5
  Size2 = 1
  SupportTransform = false
  Suppressed = false
  UseAllEdges = false
FEATURE [PartDesign::Pocket] Pocket013  label="Back screw holes001"
  BaseFeature = -> Chamfer
  Direction = (0.455211,0,-0.890384)
  Length = 5
  Length2 = 5
  Midplane = true
  Placement = pos=(156,0,0) rot=(0.57735,0.57735,0.57735;2.0944rad)
  Profile = -> Binder016
  Suppressed = false
  Type = 1
FEATURE [Sketcher::SketchObject] Sketch035  label="Back screw flats sketch"
  ArcFitTolerance = 0
  AttachmentOffset = pos=(0,0,-2) rot=(0,0,1;0rad)
  AttachmentSupport = -> [Pocket013]
  ExternalGeometry = -> [Pocket013]
  FullyConstrained = false
  MakeInternals = false
  MapMode = 5
  Placement = pos=(120.92,-2.487e-13,68.5269) rot=(0.228183,-0.228183,-0.946501;1.62575rad)
  sketch-geometry (18):
    g0: ArcOfCircle CenterX=9.73 CenterY=-126.149 CenterZ=0 NormalX=0 NormalY=0 NormalZ=1 AngleXU=0 Radius=1 StartAngle=1.5708 EndAngle=3.14159
    g1: LineSegment StartX=9.73 StartY=-125.149 StartZ=0 EndX=14.23 EndY=-125.149 EndZ=0
    g2: ArcOfCircle CenterX=14.23 CenterY=-126.149 CenterZ=0 NormalX=0 NormalY=0 NormalZ=1 AngleXU=0 Radius=1 StartAngle=-1.8e-15 EndAngle=1.5708
    g3: LineSegment StartX=15.23 StartY=-126.149 StartZ=0 EndX=15.23 EndY=-130.649 EndZ=0
    g4: ArcOfCircle CenterX=14.23 CenterY=-130.649 CenterZ=0 NormalX=0 NormalY=0 NormalZ=1 AngleXU=0 Radius=1 StartAngle=4.71239 EndAngle=6.28319
    g5: LineSegment StartX=14.23 StartY=-131.649 StartZ=0 EndX=9.73 EndY=-131.649 EndZ=0
    g6: ArcOfCircle CenterX=9.73 CenterY=-130.649 CenterZ=0 NormalX=0 NormalY=0 NormalZ=1 AngleXU=0 Radius=1 StartAngle=3.14159 EndAngle=4.71239
    g7: LineSegment StartX=8.73 StartY=-130.649 StartZ=0 EndX=8.73 EndY=-126.149 EndZ=0
    g8: ArcOfCircle CenterX=79.77 CenterY=-126.149 CenterZ=0 NormalX=0 NormalY=0 NormalZ=1 AngleXU=0 Radius=1 StartAngle=1.5708 EndAngle=3.14159
    g9: LineSegment StartX=79.77 StartY=-125.149 StartZ=0 EndX=84.27 EndY=-125.149 EndZ=0
    g10: ArcOfCircle CenterX=84.27 CenterY=-126.149 CenterZ=0 NormalX=0 NormalY=0 NormalZ=1 AngleXU=0 Radius=1 StartAngle=-6.2e-15 EndAngle=1.5708
    g11: LineSegment StartX=85.27 StartY=-126.149 StartZ=0 EndX=85.27 EndY=-130.649 EndZ=0
    g12: ArcOfCircle CenterX=84.27 CenterY=-130.649 CenterZ=0 NormalX=0 NormalY=0 NormalZ=1 AngleXU=0 Radius=1 StartAngle=4.71239 EndAngle=6.28319
    g13: LineSegment StartX=84.27 StartY=-131.649 StartZ=0 EndX=79.77 EndY=-131.649 EndZ=0
    g14: ArcOfCircle CenterX=79.77 CenterY=-130.649 CenterZ=0 NormalX=0 NormalY=0 NormalZ=1 AngleXU=0 Radius=1 StartAngle=3.14159 EndAngle=4.71239
    g15: LineSegment StartX=78.77 StartY=-130.649 StartZ=0 EndX=78.77 EndY=-126.149 EndZ=0
    g16: GeomPoint X=82.02 Y=-128.399 Z=0
    g17: GeomPoint X=11.98 Y=-128.399 Z=0
  constraints (41):
    c: Tangent(g0,g1) = 1.5708
    c: Tangent(g1,g2) = 1.5708
    c: Tangent(g2,g3) = 1.5708
    c: Tangent(g3,g4) = 1.5708
    c: Tangent(g4,g5) = 1.5708
    c: Tangent(g5,g6) = 1.5708
    c: Tangent(g6,g7) = 1.5708
    c: Tangent(g7,g0) = 1.5708
    c: Horizontal(g1)
    c: Horizontal(g5)
    c: Vertical(g3)
    c: Vertical(g7)
    c: Equal(g0,g2)
    c: Equal(g2,g4)
    c: Equal(g4,g6)
    c: Tangent(g8,g9) = 1.5708
    c: Tangent(g9,g10) = 1.5708
    c: Tangent(g10,g11) = 1.5708
    c: Tangent(g11,g12) = 1.5708
    c: Tangent(g12,g13) = 1.5708
    c: Tangent(g13,g14) = 1.5708
    c: Tangent(g14,g15) = 1.5708
    c: Tangent(g15,g8) = 1.5708
    c: Horizontal(g9)
    c: Horizontal(g13)
    c: Vertical(g11)
    c: Vertical(g15)
    c: Equal(g8,g10)
    c: Equal(g10,g12)
    c: Equal(g12,g14)
    c: Equal(g1,g3)
    c: Equal(g9,g11)
    c: Equal(g1,g9)
    c: DistanceX(g6,g3) = 6.5
    c: Equal(g2,g10)
    c: Diameter(g2) = 2
    c: Symmetric(g12,g8,g16)
    c: Symmetric(g4,g0,g17)
    c: DistanceY(g-3,g16) = 2.16
    c: Horizontal(g16,g17)
    c: DistanceX(g17,g16) = 70.04
FEATURE [PartDesign::Pocket] Pocket014  label="Back screw flats"
  BaseFeature = -> Pocket013
  Direction = (0.455678,3.3e-15,-0.890145)
  Length = 5
  Length2 = 5
  Placement = pos=(156,0,0) rot=(0.57735,0.57735,0.57735;2.0944rad)
  Profile = -> Sketch035
  ReferenceAxis = -> Sketch035 [N_Axis]
  Suppressed = false
  Type = 1
FEATURE [Sketcher::SketchObject] Sketch036  label="Front screw flats sketch"
  ArcFitTolerance = 0
  AttachmentOffset = pos=(0,0,-5.5) rot=(0,0,1;0rad)
  AttachmentSupport = -> [Pad004]
  ExternalGeometry = -> [Pocket014]
  FullyConstrained = true
  MakeInternals = false
  MapMode = 5
  Placement = pos=(157.798,9e-16,9.27155) rot=(-0.095208,0.095208,-0.990894;1.57994rad)
  sketch-geometry (17):
    g0: ArcOfCircle CenterX=72.85 CenterY=-4.14856 CenterZ=0 NormalX=0 NormalY=0 NormalZ=1 AngleXU=0 Radius=1 StartAngle=1.5708 EndAngle=3.14159
    g1: LineSegment StartX=72.85 StartY=-3.14856 StartZ=0 EndX=77.35 EndY=-3.14856 EndZ=0
    g2: ArcOfCircle CenterX=77.35 CenterY=-4.14856 CenterZ=0 NormalX=0 NormalY=0 NormalZ=1 AngleXU=0 Radius=1 StartAngle=0 EndAngle=1.5708
    g3: LineSegment StartX=78.35 StartY=-4.14856 StartZ=0 EndX=78.35 EndY=-8.64856 EndZ=0
    g4: ArcOfCircle CenterX=77.35 CenterY=-8.64856 CenterZ=0 NormalX=0 NormalY=0 NormalZ=1 AngleXU=0 Radius=1 StartAngle=4.71239 EndAngle=6.28319
    g5: LineSegment StartX=77.35 StartY=-9.64856 StartZ=0 EndX=72.85 EndY=-9.64856 EndZ=0
    g6: ArcOfCircle CenterX=72.85 CenterY=-8.64856 CenterZ=0 NormalX=0 NormalY=0 NormalZ=1 AngleXU=0 Radius=1 StartAngle=3.14159 EndAngle=4.71239
    g7: LineSegment StartX=71.85 StartY=-8.64856 StartZ=0 EndX=71.85 EndY=-4.14856 EndZ=0
    g8: GeomPoint [constr] X=78.35 Y=-9.64856 Z=0
    g9: ArcOfCircle CenterX=16.65 CenterY=-4.14856 CenterZ=0 NormalX=0 NormalY=0 NormalZ=1 AngleXU=0 Radius=1 StartAngle=1.5708 EndAngle=3.14159
    g10: LineSegment StartX=16.65 StartY=-3.14856 StartZ=0 EndX=21.15 EndY=-3.14856 EndZ=0
    g11: ArcOfCircle CenterX=21.15 CenterY=-4.14856 CenterZ=0 NormalX=0 NormalY=0 NormalZ=1 AngleXU=0 Radius=1 StartAngle=4e-16 EndAngle=1.5708
    g12: LineSegment StartX=22.15 StartY=-4.14856 StartZ=0 EndX=22.15 EndY=-8.64856 EndZ=0
    g13: ArcOfCircle CenterX=21.15 CenterY=-8.64856 CenterZ=0 NormalX=0 NormalY=0 NormalZ=1 AngleXU=0 Radius=1 StartAngle=4.71239 EndAngle=6.28319
    g14: LineSegment StartX=21.15 StartY=-9.64856 StartZ=0 EndX=16.65 EndY=-9.64856 EndZ=0
    g15: ArcOfCircle CenterX=16.65 CenterY=-8.64856 CenterZ=0 NormalX=0 NormalY=0 NormalZ=1 AngleXU=0 Radius=1 StartAngle=3.14159 EndAngle=4.71239
    g16: LineSegment StartX=15.65 StartY=-8.64856 StartZ=0 EndX=15.65 EndY=-4.14856 EndZ=0
  constraints (40):
    c: Tangent(g0,g1) = 1.5708
    c: Tangent(g1,g2) = 1.5708
    c: Tangent(g2,g3) = 1.5708
    c: Tangent(g3,g4) = 1.5708
    c: Tangent(g4,g5) = 1.5708
    c: Tangent(g5,g6) = 1.5708
    c: Tangent(g6,g7) = 1.5708
    c: Tangent(g7,g0) = 1.5708
    c: Horizontal(g1)
    c: Horizontal(g5)
    c: Vertical(g3)
    c: Vertical(g7)
    c: Equal(g0,g2)
    c: Equal(g2,g4)
    c: Equal(g4,g6)
    c: PointOnObject(g8,g3)
    c: PointOnObject(g8,g5)
    c: Equal(g1,g3)
    c: Diameter(g2) = 2
    c: Tangent(g9,g10) = 1.5708
    c: Tangent(g10,g11) = 1.5708
    c: Tangent(g11,g12) = 1.5708
    c: Tangent(g12,g13) = 1.5708
    c: Tangent(g13,g14) = 1.5708
    c: Tangent(g14,g15) = 1.5708
    c: Tangent(g15,g16) = 1.5708
    c: Tangent(g16,g9) = 1.5708
    c: Horizontal(g10)
    c: Horizontal(g14)
    c: Vertical(g12)
    c: Vertical(g16)
    c: Equal(g9,g11)
    c: Equal(g11,g13)
    c: Equal(g13,g15)
    c: Equal(g10,g12)
    c: Equal(g2,g11) = 2
    c: DistanceX(g9,g11) = 6.5
    c: Equal(g10,g1)
    c: Symmetric(g13,g9,g-4)
    c: Symmetric(g4,g0,g-3)
FEATURE [PartDesign::Pocket] Pocket015  label="Front screw flats"
  BaseFeature = -> Pocket014
  Direction = (-0.190408,0,-0.981705)
  Length = 5
  Length2 = 5
  Placement = pos=(156,0,0) rot=(0.57735,0.57735,0.57735;2.0944rad)
  Profile = -> Sketch036
  ReferenceAxis = -> Sketch036 [N_Axis]
  Refine = true
  Suppressed = false
  Type = 1
FEATURE [Sketcher::SketchObject] Sketch037  label="Rubber feet sketch"
  ArcFitTolerance = 0
  AttachmentSupport = -> [Pad007]
  ExternalGeometry = -> [Pocket015]
  FullyConstrained = true
  MakeInternals = false
  MapMode = 5
  Placement = pos=(156,-4.2e-15,8.45) rot=(0.707107,0.707107,0;3.14159rad)
  sketch-geometry (19):
    g0: LineSegment StartX=-75.77 StartY=-147 StartZ=0 EndX=-75.77 EndY=-150 EndZ=0
    g1: LineSegment StartX=-75.77 StartY=-150 StartZ=0 EndX=-65.77 EndY=-150 EndZ=0
    g2: LineSegment StartX=-65.77 StartY=-150 StartZ=0 EndX=-65.77 EndY=-147 EndZ=0
    g3: LineSegment StartX=-65.77 StartY=-147 StartZ=0 EndX=-75.77 EndY=-147 EndZ=0
    g4: LineSegment StartX=-28.23 StartY=-147 StartZ=0 EndX=-28.23 EndY=-150 EndZ=0
    g5: LineSegment StartX=-28.23 StartY=-150 StartZ=0 EndX=-18.23 EndY=-150 EndZ=0
    g6: LineSegment StartX=-18.23 StartY=-150 StartZ=0 EndX=-18.23 EndY=-147 EndZ=0
    g7: LineSegment StartX=-18.23 StartY=-147 StartZ=0 EndX=-28.23 EndY=-147 EndZ=0
    g8: LineSegment StartX=-68.85 StartY=-6.04998 StartZ=0 EndX=-68.85 EndY=-9.04998 EndZ=0
    g9: LineSegment StartX=-68.85 StartY=-9.04998 StartZ=0 EndX=-58.85 EndY=-9.04998 EndZ=0
    g10: LineSegment StartX=-58.85 StartY=-9.04998 StartZ=0 EndX=-58.85 EndY=-6.04998 EndZ=0
    g11: LineSegment StartX=-58.85 StartY=-6.04998 StartZ=0 EndX=-68.85 EndY=-6.04998 EndZ=0
    g12: GeomPoint X=-47 Y=-5.04998 Z=0
    g13: GeomPoint X=-47 Y=-151 Z=0
    g14: LineSegment [constr] StartX=-47 StartY=-5.04998 StartZ=0 EndX=-47 EndY=-151 EndZ=0
    g15: LineSegment StartX=-35.15 StartY=-6.04998 StartZ=0 EndX=-35.15 EndY=-9.04998 EndZ=0
    g16: LineSegment StartX=-35.15 StartY=-9.04998 StartZ=0 EndX=-25.15 EndY=-9.04998 EndZ=0
    g17: LineSegment StartX=-25.15 StartY=-9.04998 StartZ=0 EndX=-25.15 EndY=-6.04998 EndZ=0
    g18: LineSegment StartX=-25.15 StartY=-6.04998 StartZ=0 EndX=-35.15 EndY=-6.04998 EndZ=0
  constraints (50):
    c: Coincident(g0,g1)
    c: Coincident(g1,g2)
    c: Coincident(g2,g3)
    c: Coincident(g3,g0)
    c: Vertical(g0)
    c: Vertical(g2)
    c: Horizontal(g1)
    c: Horizontal(g3)
    c: Coincident(g4,g5)
    c: Coincident(g5,g6)
    c: Coincident(g6,g7)
    c: Coincident(g7,g4)
    c: Vertical(g4)
    c: Vertical(g6)
    c: Horizontal(g5)
    c: Horizontal(g7)
    c: Coincident(g8,g9)
    c: Coincident(g9,g10)
    c: Coincident(g10,g11)
    c: Coincident(g11,g8)
    c: Vertical(g8)
    c: Vertical(g10)
    c: Horizontal(g9)
    c: Horizontal(g11)
    c: DistanceY(g0,g0) = 3
    c: Horizontal(g1,g4)
    c: Equal(g0,g8)
    c: Equal(g1,g5)
    c: Symmetric(g-4,g-4,g12)
    c: Symmetric(g-3,g-3,g13)
    c: Coincident(g14,g12)
    c: Coincident(g14,g13)
    c: Symmetric(g2,g4,g14)
    c: Coincident(g15,g16)
    c: Coincident(g16,g17)
    c: Coincident(g17,g18)
    c: Coincident(g18,g15)
    c: Vertical(g15)
    c: Vertical(g17)
    c: Horizontal(g16)
    c: Horizontal(g18)
    c: Horizontal(g10,g15)
    c: DistanceX(g1,g1) = 10
    c: DistanceX(g-3,g0) = 3
    c: DistanceY(g-3,g0) = 1
    c: DistanceY(g8,g-4) = 1
    c: DistanceX(g-4,g8) = 3
    c: Equal(g1,g9)
    c: Equal(g9,g16)
    c: Symmetric(g8,g16,g14)
FEATURE [PartDesign::Pocket] Pocket016  label="Rubber feet"
  BaseFeature = -> Pocket015
  Direction = (0,0,1)
  Length = 0.5
  Length2 = 5
  Placement = pos=(156,0,0) rot=(0.57735,0.57735,0.57735;2.0944rad)
  Profile = -> Sketch037
  ReferenceAxis = -> Sketch037 [N_Axis]
  Suppressed = false
  Type = 0
FEATURE [PartDesign::Fillet] Fillet002  label="Support column fillets"
  Base = -> Pocket016 [Edge214,Edge213,Edge216,Edge217,Edge215]
  BaseFeature = -> Pocket016
  Placement = pos=(156,0,0) rot=(0.57735,0.57735,0.57735;2.0944rad)
  Radius = 3
  SupportTransform = false
  Suppressed = false
  UseAllEdges = false
FEATURE [PartDesign::Chamfer] Chamfer001  label="Support column top chamfer"
  Angle = 45
  Base = -> Fillet002 [Edge223,Edge95,Edge225,Edge227,Edge229]
  BaseFeature = -> Fillet002
  ChamferType = 0
  FlipDirection = false
  Placement = pos=(156,0,0) rot=(0.57735,0.57735,0.57735;2.0944rad)
  Size = 0.5
  Size2 = 1
  SupportTransform = false
  Suppressed = false
  UseAllEdges = false
FEATURE [PartDesign::Body] Body001  label="EnclosureBottomBody"
  AllowCompound = false
  Group = -> [DatumPlane005,Sketch010,Pad004,Binder007,Sketch011,Sketch012,AdditiveLoft,Sketch013,Binder011,Sketch014,Sketch015,Pad005,Pad006,Pad007,Binder013,Sketch017,Sketch018,Sketch019,DatumPlane009,Sketch020,Binder014,DatumPlane012,DatumPlane014,Sketch021,Sketch022,SubtractiveLoft,DatumPlane015,Sketch024,DatumPoint004,DatumPoint005,DatumLine007,Sketch025,Sketch026,Pad008,Sketch027,Pocket006,Sketch028,+26 more]
  Origin = -> Origin004
  Tip = -> Chamfer001
FEATURE [App::Part] Part001  label="EnclosureBottom"
  Group = -> [Body001]
  Origin = -> Origin003
